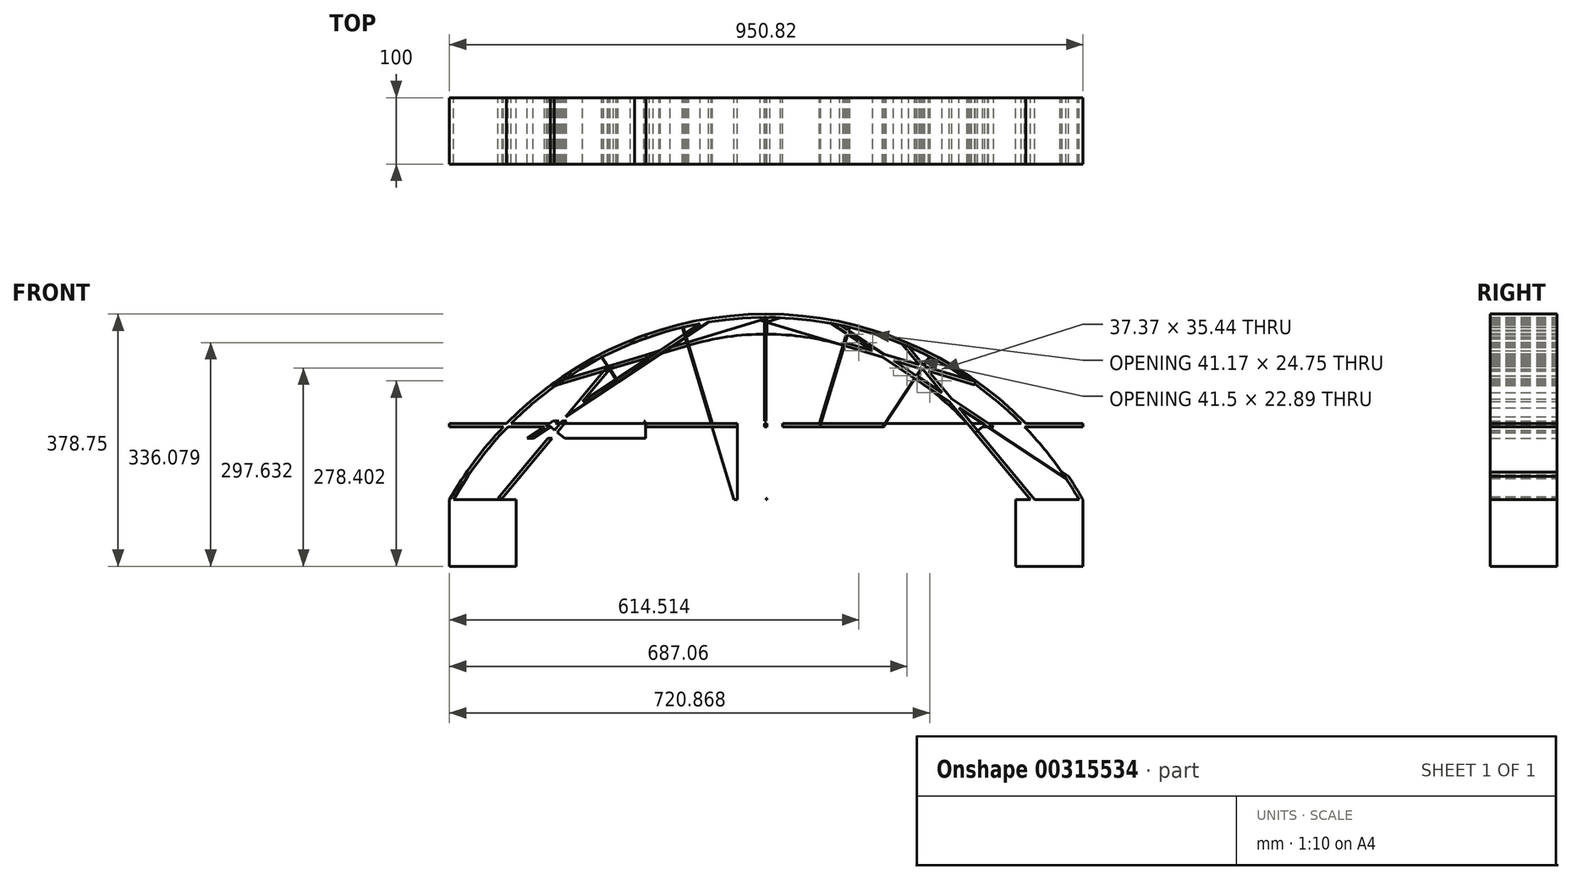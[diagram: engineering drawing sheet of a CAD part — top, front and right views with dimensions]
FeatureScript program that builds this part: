
annotation { "Feature Type Name" : "Feature", "Feature Type Description" : "" }
export const myFeature = defineFeature(function(context is Context, id is Id, definition is map)
    precondition{}
    {
        {
            var Q0;
            Q0=qCreatedBy(makeId("Front.planeOp"),FACE);
            var sketch = newSketch(context, id + "F0", { "sketchPlane" : qUnion([Q0])});
            skLineSegment(sketch, "E0.bottom", {"start": v(0, 85.96) * mm, "end": v(-100, 85.96) * mm});
            skLineSegment(sketch, "E0.top", {"start": v(0, 185.96) * mm, "end": v(-100, 185.96) * mm});
            skLineSegment(sketch, "E0.left", {"start": v(0, 85.96) * mm, "end": v(0, 185.96) * mm});
            skLineSegment(sketch, "E0.right", {"start": v(-100, 85.96) * mm, "end": v(-100, 185.96) * mm});
            skPoint(sketch, "E0.middle", {"position": v(-50, 135.96) * mm});
            skLineSegment(sketch, "E1", {"start": v(0, 185.96) * mm, "end": v(375, 185.96) * mm});
            skLineSegment(sketch, "E2", {"start": v(375, 185.96) * mm, "end": v(750, 185.96) * mm});
            skLineSegment(sketch, "E3.bottom", {"start": v(750, 185.96) * mm, "end": v(850.82, 185.96) * mm});
            skLineSegment(sketch, "E3.top", {"start": v(750, 85.96) * mm, "end": v(850.82, 85.96) * mm});
            skLineSegment(sketch, "E3.left", {"start": v(750, 185.96) * mm, "end": v(750, 85.96) * mm});
            skLineSegment(sketch, "E3.right", {"start": v(850.82, 185.96) * mm, "end": v(850.82, 85.96) * mm});
            skArc(sketch, "E4", {"start": v(750, 185.96) * mm, "mid": v(375, 434.6) * mm, "end": v(0, 185.96) * mm});
            skArc(sketch, "E5", {"start": v(850.82, 185.96) * mm, "mid": v(375.41, 464.71) * mm, "end": v(-100, 185.96) * mm});
            skLineSegment(sketch, "E6", {"start": v(-100, 295.5) * mm, "end": v(850.82, 295.5) * mm});
            skLineSegment(sketch, "E7", {"start": v(850.82, 295.5) * mm, "end": v(850.82, 300.5) * mm});
            skLineSegment(sketch, "E8", {"start": v(850.82, 300.5) * mm, "end": v(-100, 300.5) * mm});
            skLineSegment(sketch, "E9", {"start": v(-100, 300.5) * mm, "end": v(-100, 295.5) * mm});
            skLineSegment(sketch, "E10", {"start": v(375, 27.5) * mm, "end": v(325, 27.5) * mm});
            skLineSegment(sketch, "E11", {"start": v(375, 27.5) * mm, "end": v(425, 27.5) * mm});
            skLineSegment(sketch, "E12", {"start": v(375, 27.5) * mm, "end": v(0, 185.96) * mm});
            skLineSegment(sketch, "E13", {"start": v(375, 27.5) * mm, "end": v(318.99, 73.97) * mm});
            skLineSegment(sketch, "E14", {"start": v(375, 27.5) * mm, "end": v(339.38, 81.23) * mm});
            skLineSegment(sketch, "E15", {"start": v(375, 27.5) * mm, "end": v(354.37, 95.94) * mm});
            skLineSegment(sketch, "E16", {"start": v(375, 27.5) * mm, "end": v(375, 108.9) * mm});
            skLineSegment(sketch, "E17", {"start": v(318.99, 73.97) * mm, "end": v(13.67, 327.28) * mm});
            skLineSegment(sketch, "E18", {"start": v(339.38, 81.23) * mm, "end": v(125.4, 403.95) * mm});
            skLineSegment(sketch, "E19", {"start": v(354.37, 95.94) * mm, "end": v(247.79, 449.55) * mm});
            skLineSegment(sketch, "E20", {"start": v(375, 108.9) * mm, "end": v(375, 464.71) * mm});
            skLineSegment(sketch, "E21", {"start": v(61.68, 287.44) * mm, "end": v(-22.5, 185.96) * mm});
            skLineSegment(sketch, "E22", {"start": v(61.68, 287.44) * mm, "end": v(178.05, 427.7) * mm});
            skLineSegment(sketch, "E23", {"start": v(150.03, 366.8) * mm, "end": v(-85.2, 210.82) * mm});
            skLineSegment(sketch, "E24", {"start": v(257.51, 417.29) * mm, "end": v(45.34, 353.33) * mm});
            skLineSegment(sketch, "E25", {"start": v(257.51, 417.29) * mm, "end": v(411, 463.55) * mm});
            skLineSegment(sketch, "E26", {"start": v(375, 452.7) * mm, "end": v(706.03, 352.92) * mm});
            skLineSegment(sketch, "E27", {"start": v(375, 452.7) * mm, "end": v(339.15, 463.5) * mm});
            skLineSegment(sketch, "E28", {"start": v(572.77, 427.7) * mm, "end": v(771.91, 185.96) * mm});
            skLineSegment(sketch, "E29", {"start": v(836.03, 210.82) * mm, "end": v(462.36, 457.73) * mm});
            skLineSegment(sketch, "E30", {"start": v(492.49, 417.29) * mm, "end": v(375, 27.5) * mm});
            skLineSegment(sketch, "E31", {"start": v(375, 27.5) * mm, "end": v(624.17, 404.6) * mm});
            skLineSegment(sketch, "E32", {"start": v(375, 27.5) * mm, "end": v(738, 326.53) * mm});
            skLineSegment(sketch, "E33", {"start": v(375, 27.5) * mm, "end": v(750, 185.96) * mm});
            skLineSegment(sketch, "E34", {"start": v(-22.5, 185.96) * mm, "end": v(-26.35, 189.15) * mm});
            skLineSegment(sketch, "E35", {"start": v(-26.35, 189.15) * mm, "end": v(168.33, 423.82) * mm});
            skLineSegment(sketch, "E36", {"start": v(168.33, 423.82) * mm, "end": v(-29, 185.96) * mm});
            skLineSegment(sketch, "E37", {"start": v(-85.2, 210.82) * mm, "end": v(-82.44, 206.66) * mm});
            skLineSegment(sketch, "E38", {"start": v(-82.44, 206.66) * mm, "end": v(298.52, 459.26) * mm});
            skLineSegment(sketch, "E39", {"start": v(150.03, 366.8) * mm, "end": v(286.74, 457.45) * mm});
            skLineSegment(sketch, "E40", {"start": v(-82.44, 206.66) * mm, "end": v(-91.46, 200.68) * mm});
            skLineSegment(sketch, "E41", {"start": v(69.56, 360.64) * mm, "end": v(68.12, 365.42) * mm});
            skLineSegment(sketch, "E42", {"start": v(68.12, 365.42) * mm, "end": v(396.21, 464.32) * mm});
            skLineSegment(sketch, "E43", {"start": v(396.21, 464.32) * mm, "end": v(57.23, 362.14) * mm});
            skLineSegment(sketch, "E44", {"start": v(688.37, 358.25) * mm, "end": v(689.8, 363.03) * mm});
            skLineSegment(sketch, "E45", {"start": v(689.8, 363.03) * mm, "end": v(694.18, 361.72) * mm});
            skLineSegment(sketch, "E46", {"start": v(694.18, 361.72) * mm, "end": v(353.88, 464.29) * mm});
            skLineSegment(sketch, "E47", {"start": v(816.74, 223.57) * mm, "end": v(819.5, 227.74) * mm});
            skLineSegment(sketch, "E48", {"start": v(819.5, 227.74) * mm, "end": v(829.25, 221.3) * mm});
            skLineSegment(sketch, "E49", {"start": v(829.25, 221.3) * mm, "end": v(474.65, 455.6) * mm});
            skLineSegment(sketch, "E50", {"start": v(763.23, 196.5) * mm, "end": v(767.1, 199.68) * mm});
            skLineSegment(sketch, "E51", {"start": v(767.1, 199.68) * mm, "end": v(778.4, 185.96) * mm});
            skLineSegment(sketch, "E52", {"start": v(778.4, 185.96) * mm, "end": v(582.43, 423.85) * mm});
            skLineSegment(sketch, "E53", {"start": v(0, 185.96) * mm, "end": v(-4.6, 187.9) * mm});
            skLineSegment(sketch, "E54", {"start": v(750, 185.96) * mm, "end": v(754.6, 187.9) * mm});
            skLineSegment(sketch, "E55", {"start": v(-98.5, 188.61) * mm, "end": v(-94.02, 186.4) * mm});
            skLineSegment(sketch, "E56", {"start": v(375, 464.71) * mm, "end": v(375, 459.71) * mm});
            skLineSegment(sketch, "E57", {"start": v(846.68, 193.24) * mm, "end": v(842.5, 190.5) * mm});
            skArc(sketch, "E58", {"start": v(842.5, 190.5) * mm, "mid": v(373.05, 459.7) * mm, "end": v(-94.02, 186.4) * mm});
            skLineSegment(sketch, "E59", {"start": v(842.5, 190.5) * mm, "end": v(845.47, 185.96) * mm});
            skLineSegment(sketch, "E60", {"start": v(-94.02, 186.4) * mm, "end": v(-94.24, 185.96) * mm});
            skLineSegment(sketch, "E61", {"start": v(372.99, 188.16) * mm, "end": v(376.3, 188.16) * mm});
            skLineSegment(sketch, "E62", {"start": v(376.3, 188.16) * mm, "end": v(376.3, 464.71) * mm});
            skLineSegment(sketch, "E63", {"start": v(376.3, 464.71) * mm, "end": v(376.3, 185.96) * mm});
            skLineSegment(sketch, "E64", {"start": v(376.3, 185.96) * mm, "end": v(372.99, 185.96) * mm});
            skLineSegment(sketch, "E65", {"start": v(372.99, 185.96) * mm, "end": v(372.99, 464.7) * mm});
            skLineSegment(sketch, "E66", {"start": v(420.7, 185.96) * mm, "end": v(500.35, 450.2) * mm});
            skLineSegment(sketch, "E67", {"start": v(492.49, 417.29) * mm, "end": v(502.4, 450.2) * mm});
            skLineSegment(sketch, "E68", {"start": v(477.93, 185.96) * mm, "end": v(622.85, 405.28) * mm});
            skLineSegment(sketch, "E69", {"start": v(294.52, 300.5) * mm, "end": v(249.59, 449.55) * mm});
            skLineSegment(sketch, "E70", {"start": v(194.9, 300.5) * mm, "end": v(126.07, 404.3) * mm});
            skLineSegment(sketch, "E71", {"start": v(400, 27.5) * mm, "end": v(400, 434.6) * mm});
            skPoint(sketch, "E71.endSnap0", {"position": v(375, 434.6) * mm});
            skLineSegment(sketch, "E72", {"start": v(415.27, 434.6) * mm, "end": v(415.27, 185.96) * mm});
            skLineSegment(sketch, "E73", {"start": v(194.97, -80.07) * mm, "end": v(194.97, 464.71) * mm});
            skLineSegment(sketch, "E74", {"start": v(292.72, 300.5) * mm, "end": v(292.72, 278.2) * mm});
            skLineSegment(sketch, "E75", {"start": v(375, 278.2) * mm, "end": v(292.72, 278.2) * mm});
            skLineSegment(sketch, "E76", {"start": v(194, 300.5) * mm, "end": v(194, 278.2) * mm});
            skLineSegment(sketch, "E77", {"start": v(292.72, 278.2) * mm, "end": v(194, 278.2) * mm});
            skLineSegment(sketch, "E78", {"start": v(45.95, 300.5) * mm, "end": v(45.95, 278.2) * mm});
            skLineSegment(sketch, "E79", {"start": v(45.95, 278.2) * mm, "end": v(194, 278.2) * mm});
            skLineSegment(sketch, "E80", {"start": v(-100, 295.5) * mm, "end": v(-100, 278.2) * mm});
            skLineSegment(sketch, "E81", {"start": v(-100, 278.2) * mm, "end": v(45.95, 278.2) * mm});
            skLineSegment(sketch, "E82", {"start": v(332.4, 300.5) * mm, "end": v(332.4, 185.96) * mm});
            skLineSegment(sketch, "E83", {"start": v(375, 304.05) * mm, "end": v(-10.9, 304.05) * mm});
            skLineSegment(sketch, "E84", {"start": v(-22.5, 189.52) * mm, "end": v(0, 189.52) * mm});
            skLineSegment(sketch, "E85", {"start": v(-82.44, 188.18) * mm, "end": v(0, 188.18) * mm});
            skLineSegment(sketch, "E86", {"start": v(60.02, 358) * mm, "end": v(0, 358) * mm});
            skSolve(sketch);
        }
        {
            var Q0;
            {var subQ5=sQuery(id+"F0.wireOp",EDGE,"E7");Q0=makeQuery(id+"F0.imprint","IMPRINT",FACE,{"disambiguationData":[TD([[makeQuery(id+"F0.imprint","IMPRINT",EDGE,{"derivedFrom":subQ5}),1.0]])]});}
            var Q1;
            {var subQ5=sQuery(id+"F0.wireOp",EDGE,"E9");Q1=makeQuery(id+"F0.imprint","IMPRINT",FACE,{"disambiguationData":[TD([[makeQuery(id+"F0.imprint","IMPRINT",EDGE,{"derivedFrom":subQ5}),1.0]])]});}
            var Q2;
            {var subQ0=sQuery(id+"F0.wireOp",EDGE,"E37");Q2=makeQuery(id+"F0.imprint","IMPRINT",FACE,{"disambiguationData":[TD([[makeQuery(id+"F0.imprint","IMPRINT",EDGE,{"derivedFrom":subQ0}),-1.0]])]});}
            var Q3;
            {var subQ4=sQuery(id+"F0.wireOp",EDGE,"E55");Q3=makeQuery(id+"F0.imprint","IMPRINT",FACE,{"disambiguationData":[TD([[makeQuery(id+"F0.imprint","IMPRINT",EDGE,{"derivedFrom":subQ4}),-1.0]])]});}
            var Q4;
            {var subQ4=sQuery(id+"F0.wireOp",EDGE,"E57");Q4=makeQuery(id+"F0.imprint","IMPRINT",FACE,{"disambiguationData":[TD([[makeQuery(id+"F0.imprint","IMPRINT",EDGE,{"derivedFrom":subQ4}),1.0]])]});}
            var Q5;
            {var subQ3=sQuery(id+"F0.wireOp",EDGE,"E57");Q5=makeQuery(id+"F0.imprint","IMPRINT",FACE,{"disambiguationData":[TD([[makeQuery(id+"F0.imprint","IMPRINT",EDGE,{"derivedFrom":subQ3}),-1.0]])]});}
            var Q6;
            {var subQ0=sQuery(id+"F0.wireOp",EDGE,"E32");var subQ1=sQuery(id+"F0.wireOp",EDGE,"E5");var subQ2=makeQuery(id+"F0.imprint","INTERSECT",VERTEX,{"derivedFrom":[subQ1,subQ0]});Q6=makeQuery(id+"F0.imprint","IMPRINT",FACE,{"disambiguationData":[TD([[makeQuery(id+"F0.imprint","IMPRINT",EDGE,{"disambiguationData":[TD([[subQ2,1.0]])],"derivedFrom":subQ1}),1.0]])]});}
            var Q7;
            {var subQ0=sQuery(id+"F0.wireOp",EDGE,"E26");var subQ1=sQuery(id+"F0.wireOp",EDGE,"E5");var subQ2=makeQuery(id+"F0.imprint","INTERSECT",VERTEX,{"derivedFrom":[subQ1,subQ0]});Q7=makeQuery(id+"F0.imprint","IMPRINT",FACE,{"disambiguationData":[TD([[makeQuery(id+"F0.imprint","IMPRINT",EDGE,{"disambiguationData":[TD([[subQ2,1.0]])],"derivedFrom":subQ1}),1.0]])]});}
            var Q8;
            {var subQ0=sQuery(id+"F0.wireOp",EDGE,"E31");var subQ1=sQuery(id+"F0.wireOp",EDGE,"E5");var subQ2=makeQuery(id+"F0.imprint","INTERSECT",VERTEX,{"derivedFrom":[subQ1,subQ0]});Q8=makeQuery(id+"F0.imprint","IMPRINT",FACE,{"disambiguationData":[TD([[makeQuery(id+"F0.imprint","IMPRINT",EDGE,{"disambiguationData":[TD([[subQ2,-1.0]])],"derivedFrom":subQ1}),1.0]])]});}
            var Q9;
            {var subQ0=sQuery(id+"F0.wireOp",EDGE,"E52");var subQ1=sQuery(id+"F0.wireOp",EDGE,"E5");var subQ2=makeQuery(id+"F0.imprint","INTERSECT",VERTEX,{"derivedFrom":[subQ1,subQ0]});Q9=makeQuery(id+"F0.imprint","IMPRINT",FACE,{"disambiguationData":[TD([[makeQuery(id+"F0.imprint","IMPRINT",EDGE,{"disambiguationData":[TD([[subQ2,1.0]])],"derivedFrom":subQ1}),1.0]])]});}
            var Q10;
            {var subQ0=sQuery(id+"F0.wireOp",EDGE,"E28");var subQ1=sQuery(id+"F0.wireOp",EDGE,"E5");var subQ2=makeQuery(id+"F0.imprint","INTERSECT",VERTEX,{"derivedFrom":[subQ1,subQ0]});Q10=makeQuery(id+"F0.imprint","IMPRINT",FACE,{"disambiguationData":[TD([[makeQuery(id+"F0.imprint","IMPRINT",EDGE,{"disambiguationData":[TD([[subQ2,1.0]])],"derivedFrom":subQ1}),1.0]])]});}
            var Q11;
            {var subQ0=sQuery(id+"F0.wireOp",EDGE,"E28");var subQ1=sQuery(id+"F0.wireOp",EDGE,"E5");var subQ2=makeQuery(id+"F0.imprint","INTERSECT",VERTEX,{"derivedFrom":[subQ1,subQ0]});Q11=makeQuery(id+"F0.imprint","IMPRINT",FACE,{"disambiguationData":[TD([[makeQuery(id+"F0.imprint","IMPRINT",EDGE,{"disambiguationData":[TD([[subQ2,-1.0]])],"derivedFrom":subQ1}),1.0]])]});}
            var Q12;
            {var subQ0=sQuery(id+"F0.wireOp",EDGE,"E66");var subQ1=sQuery(id+"F0.wireOp",EDGE,"E5");var subQ2=makeQuery(id+"F0.imprint","INTERSECT",VERTEX,{"derivedFrom":[subQ1,subQ0]});Q12=makeQuery(id+"F0.imprint","IMPRINT",FACE,{"disambiguationData":[TD([[makeQuery(id+"F0.imprint","IMPRINT",EDGE,{"disambiguationData":[TD([[subQ2,1.0]])],"derivedFrom":subQ1}),1.0]])]});}
            var Q13;
            {var subQ0=sQuery(id+"F0.wireOp",EDGE,"E49");var subQ1=sQuery(id+"F0.wireOp",EDGE,"E5");var subQ2=makeQuery(id+"F0.imprint","INTERSECT",VERTEX,{"disambiguationData":[OD(1.0)],"derivedFrom":[subQ1,subQ0]});Q13=makeQuery(id+"F0.imprint","IMPRINT",FACE,{"disambiguationData":[TD([[makeQuery(id+"F0.imprint","IMPRINT",EDGE,{"disambiguationData":[TD([[subQ2,1.0]])],"derivedFrom":subQ1}),1.0]])]});}
            var Q14;
            {var subQ0=sQuery(id+"F0.wireOp",EDGE,"E29");var subQ1=sQuery(id+"F0.wireOp",EDGE,"E5");var subQ2=makeQuery(id+"F0.imprint","INTERSECT",VERTEX,{"disambiguationData":[OD(1.0)],"derivedFrom":[subQ1,subQ0]});Q14=makeQuery(id+"F0.imprint","IMPRINT",FACE,{"disambiguationData":[TD([[makeQuery(id+"F0.imprint","IMPRINT",EDGE,{"disambiguationData":[TD([[subQ2,1.0]])],"derivedFrom":subQ1}),1.0]])]});}
            var Q15;
            {var subQ0=sQuery(id+"F0.wireOp",EDGE,"E25");var subQ1=sQuery(id+"F0.wireOp",EDGE,"E5");var subQ2=makeQuery(id+"F0.imprint","INTERSECT",VERTEX,{"derivedFrom":[subQ1,subQ0]});Q15=makeQuery(id+"F0.imprint","IMPRINT",FACE,{"disambiguationData":[TD([[makeQuery(id+"F0.imprint","IMPRINT",EDGE,{"disambiguationData":[TD([[subQ2,1.0]])],"derivedFrom":subQ1}),1.0]])]});}
            var Q16;
            {var subQ0=sQuery(id+"F0.wireOp",EDGE,"E25");var subQ1=sQuery(id+"F0.wireOp",EDGE,"E5");var subQ2=makeQuery(id+"F0.imprint","INTERSECT",VERTEX,{"derivedFrom":[subQ1,subQ0]});Q16=makeQuery(id+"F0.imprint","IMPRINT",FACE,{"disambiguationData":[TD([[makeQuery(id+"F0.imprint","IMPRINT",EDGE,{"disambiguationData":[TD([[subQ2,-1.0]])],"derivedFrom":subQ1}),1.0]])]});}
            var Q17;
            {var subQ0=sQuery(id+"F0.wireOp",EDGE,"E43");var subQ1=sQuery(id+"F0.wireOp",EDGE,"E5");var subQ2=makeQuery(id+"F0.imprint","INTERSECT",VERTEX,{"disambiguationData":[OD(0.0)],"derivedFrom":[subQ1,subQ0]});Q17=makeQuery(id+"F0.imprint","IMPRINT",FACE,{"disambiguationData":[TD([[makeQuery(id+"F0.imprint","IMPRINT",EDGE,{"disambiguationData":[TD([[subQ2,-1.0]])],"derivedFrom":subQ1}),1.0]])]});}
            var Q18;
            {var subQ0=sQuery(id+"F0.wireOp",EDGE,"E56");Q18=makeQuery(id+"F0.imprint","IMPRINT",FACE,{"disambiguationData":[TD([[makeQuery(id+"F0.imprint","IMPRINT",EDGE,{"derivedFrom":subQ0}),1.0]])]});}
            var Q19;
            {var subQ0=sQuery(id+"F0.wireOp",EDGE,"E56");Q19=makeQuery(id+"F0.imprint","IMPRINT",FACE,{"disambiguationData":[TD([[makeQuery(id+"F0.imprint","IMPRINT",EDGE,{"derivedFrom":subQ0}),-1.0]])]});}
            var Q20;
            {var subQ0=sQuery(id+"F0.wireOp",EDGE,"E46");var subQ1=sQuery(id+"F0.wireOp",EDGE,"E5");var subQ2=makeQuery(id+"F0.imprint","INTERSECT",VERTEX,{"disambiguationData":[OD(1.0)],"derivedFrom":[subQ1,subQ0]});Q20=makeQuery(id+"F0.imprint","IMPRINT",FACE,{"disambiguationData":[TD([[makeQuery(id+"F0.imprint","IMPRINT",EDGE,{"disambiguationData":[TD([[subQ2,1.0]])],"derivedFrom":subQ1}),1.0]])]});}
            var Q21;
            {var subQ0=sQuery(id+"F0.wireOp",EDGE,"E27");var subQ1=sQuery(id+"F0.wireOp",EDGE,"E5");var subQ2=makeQuery(id+"F0.imprint","INTERSECT",VERTEX,{"derivedFrom":[subQ1,subQ0]});Q21=makeQuery(id+"F0.imprint","IMPRINT",FACE,{"disambiguationData":[TD([[makeQuery(id+"F0.imprint","IMPRINT",EDGE,{"disambiguationData":[TD([[subQ2,1.0]])],"derivedFrom":subQ1}),1.0]])]});}
            var Q22;
            {var subQ0=sQuery(id+"F0.wireOp",EDGE,"E27");var subQ1=sQuery(id+"F0.wireOp",EDGE,"E5");var subQ2=makeQuery(id+"F0.imprint","INTERSECT",VERTEX,{"derivedFrom":[subQ1,subQ0]});Q22=makeQuery(id+"F0.imprint","IMPRINT",FACE,{"disambiguationData":[TD([[makeQuery(id+"F0.imprint","IMPRINT",EDGE,{"disambiguationData":[TD([[subQ2,-1.0]])],"derivedFrom":subQ1}),1.0]])]});}
            var Q23;
            {var subQ0=sQuery(id+"F0.wireOp",EDGE,"E38");var subQ1=sQuery(id+"F0.wireOp",EDGE,"E5");var subQ2=makeQuery(id+"F0.imprint","INTERSECT",VERTEX,{"derivedFrom":[subQ1,subQ0]});Q23=makeQuery(id+"F0.imprint","IMPRINT",FACE,{"disambiguationData":[TD([[makeQuery(id+"F0.imprint","IMPRINT",EDGE,{"disambiguationData":[TD([[subQ2,-1.0]])],"derivedFrom":subQ1}),1.0]])]});}
            var Q24;
            {var subQ0=sQuery(id+"F0.wireOp",EDGE,"E19");var subQ1=sQuery(id+"F0.wireOp",EDGE,"E5");var subQ2=makeQuery(id+"F0.imprint","INTERSECT",VERTEX,{"derivedFrom":[subQ1,subQ0]});Q24=makeQuery(id+"F0.imprint","IMPRINT",FACE,{"disambiguationData":[TD([[makeQuery(id+"F0.imprint","IMPRINT",EDGE,{"disambiguationData":[TD([[subQ2,-1.0]])],"derivedFrom":subQ1}),1.0]])]});}
            var Q25;
            {var subQ0=sQuery(id+"F0.wireOp",EDGE,"E22");var subQ1=sQuery(id+"F0.wireOp",EDGE,"E5");var subQ2=makeQuery(id+"F0.imprint","INTERSECT",VERTEX,{"derivedFrom":[subQ1,subQ0]});Q25=makeQuery(id+"F0.imprint","IMPRINT",FACE,{"disambiguationData":[TD([[makeQuery(id+"F0.imprint","IMPRINT",EDGE,{"disambiguationData":[TD([[subQ2,-1.0]])],"derivedFrom":subQ1}),1.0]])]});}
            var Q26;
            {var subQ0=sQuery(id+"F0.wireOp",EDGE,"E36");var subQ1=sQuery(id+"F0.wireOp",EDGE,"E5");var subQ2=makeQuery(id+"F0.imprint","INTERSECT",VERTEX,{"derivedFrom":[subQ1,subQ0]});Q26=makeQuery(id+"F0.imprint","IMPRINT",FACE,{"disambiguationData":[TD([[makeQuery(id+"F0.imprint","IMPRINT",EDGE,{"disambiguationData":[TD([[subQ2,-1.0]])],"derivedFrom":subQ1}),1.0]])]});}
            var Q27;
            {var subQ0=sQuery(id+"F0.wireOp",EDGE,"E18");var subQ1=sQuery(id+"F0.wireOp",EDGE,"E5");var subQ2=makeQuery(id+"F0.imprint","INTERSECT",VERTEX,{"derivedFrom":[subQ1,subQ0]});Q27=makeQuery(id+"F0.imprint","IMPRINT",FACE,{"disambiguationData":[TD([[makeQuery(id+"F0.imprint","IMPRINT",EDGE,{"disambiguationData":[TD([[subQ2,1.0]])],"derivedFrom":subQ1}),1.0]])]});}
            var Q28;
            {var subQ0=sQuery(id+"F0.wireOp",EDGE,"E17");var subQ1=sQuery(id+"F0.wireOp",EDGE,"E5");var subQ2=makeQuery(id+"F0.imprint","INTERSECT",VERTEX,{"derivedFrom":[subQ1,subQ0]});Q28=makeQuery(id+"F0.imprint","IMPRINT",FACE,{"disambiguationData":[TD([[makeQuery(id+"F0.imprint","IMPRINT",EDGE,{"disambiguationData":[TD([[subQ2,1.0]])],"derivedFrom":subQ1}),1.0]])]});}
            var Q29;
            {var subQ0=sQuery(id+"F0.wireOp",EDGE,"E17");var subQ1=sQuery(id+"F0.wireOp",EDGE,"E5");var subQ2=makeQuery(id+"F0.imprint","INTERSECT",VERTEX,{"derivedFrom":[subQ1,subQ0]});Q29=makeQuery(id+"F0.imprint","IMPRINT",FACE,{"disambiguationData":[TD([[makeQuery(id+"F0.imprint","IMPRINT",EDGE,{"disambiguationData":[TD([[subQ2,-1.0]])],"derivedFrom":subQ1}),1.0]])]});}
            var Q30;
            {var subQ1=sQuery(id+"F0.wireOp",EDGE,"E5");var subQ3=sQuery(id+"F0.wireOp",EDGE,"E6");var subQ4=makeQuery(id+"F0.imprint","INTERSECT",VERTEX,{"disambiguationData":[OD(1.0)],"derivedFrom":[subQ1,subQ3]});Q30=makeQuery(id+"F0.imprint","IMPRINT",FACE,{"disambiguationData":[TD([[makeQuery(id+"F0.imprint","IMPRINT",EDGE,{"disambiguationData":[TD([[subQ4,-1.0]])],"derivedFrom":subQ3}),-1.0]])]});}
            var Q31;
            Q31=makeQuery(id+"F0.imprint","IMPRINT",FACE,{"disambiguationData":[TD([[makeQuery(id+"F0.imprint","IMPRINT",EDGE,{"derivedFrom":sQuery(id+"F0.wireOp",EDGE,"E0.bottom")}),-1.0]])]});
            var Q32;
            Q32=makeQuery(id+"F0.imprint","IMPRINT",FACE,{"disambiguationData":[TD([[makeQuery(id+"F0.imprint","IMPRINT",EDGE,{"derivedFrom":sQuery(id+"F0.wireOp",EDGE,"E3.top")}),1.0]])]});
            var Q33;
            {var subQ3=sQuery(id+"F0.wireOp",EDGE,"E5");var subQ7=sQuery(id+"F0.wireOp",EDGE,"E29");var subQ9=makeQuery(id+"F0.imprint","INTERSECT",VERTEX,{"disambiguationData":[OD(0.0)],"derivedFrom":[subQ3,subQ7]});Q33=makeQuery(id+"F0.imprint","IMPRINT",FACE,{"disambiguationData":[TD([[makeQuery(id+"F0.imprint","IMPRINT",EDGE,{"disambiguationData":[TD([[subQ9,-1.0]])],"derivedFrom":subQ3}),1.0]])]});}
            var Q34;
            {var subQ0=sQuery(id+"F0.wireOp",EDGE,"E49");var subQ6=sQuery(id+"F0.wireOp",EDGE,"E5");var subQ7=makeQuery(id+"F0.imprint","INTERSECT",VERTEX,{"disambiguationData":[OD(0.0)],"derivedFrom":[subQ6,subQ0]});Q34=makeQuery(id+"F0.imprint","IMPRINT",FACE,{"disambiguationData":[TD([[makeQuery(id+"F0.imprint","IMPRINT",EDGE,{"disambiguationData":[TD([[subQ7,-1.0]])],"derivedFrom":subQ6}),1.0]])]});}
            var Q35;
            {var subQ0=sQuery(id+"F0.wireOp",EDGE,"E6");var subQ1=sQuery(id+"F0.wireOp",EDGE,"E5");var subQ2=makeQuery(id+"F0.imprint","INTERSECT",VERTEX,{"disambiguationData":[OD(0.0)],"derivedFrom":[subQ1,subQ0]});Q35=makeQuery(id+"F0.imprint","IMPRINT",FACE,{"disambiguationData":[TD([[makeQuery(id+"F0.imprint","IMPRINT",EDGE,{"disambiguationData":[TD([[subQ2,-1.0]])],"derivedFrom":subQ1}),1.0]])]});}
            var Q36;
            {var subQ3=sQuery(id+"F0.wireOp",EDGE,"E5");var subQ7=sQuery(id+"F0.wireOp",EDGE,"E26");var subQ8=makeQuery(id+"F0.imprint","INTERSECT",VERTEX,{"derivedFrom":[subQ3,subQ7]});Q36=makeQuery(id+"F0.imprint","IMPRINT",FACE,{"disambiguationData":[TD([[makeQuery(id+"F0.imprint","IMPRINT",EDGE,{"disambiguationData":[TD([[subQ8,-1.0]])],"derivedFrom":subQ3}),1.0]])]});}
            var Q37;
            {var subQ4=sQuery(id+"F0.wireOp",EDGE,"E5");var subQ6=sQuery(id+"F0.wireOp",EDGE,"E31");var subQ7=makeQuery(id+"F0.imprint","INTERSECT",VERTEX,{"derivedFrom":[subQ4,subQ6]});Q37=makeQuery(id+"F0.imprint","IMPRINT",FACE,{"disambiguationData":[TD([[makeQuery(id+"F0.imprint","IMPRINT",EDGE,{"disambiguationData":[TD([[subQ7,1.0]])],"derivedFrom":subQ4}),1.0]])]});}
            var Q38;
            {var subQ4=sQuery(id+"F0.wireOp",EDGE,"E19");var subQ5=sQuery(id+"F0.wireOp",EDGE,"E5");var subQ6=makeQuery(id+"F0.imprint","INTERSECT",VERTEX,{"derivedFrom":[subQ5,subQ4]});Q38=makeQuery(id+"F0.imprint","IMPRINT",FACE,{"disambiguationData":[TD([[makeQuery(id+"F0.imprint","IMPRINT",EDGE,{"disambiguationData":[TD([[subQ6,1.0]])],"derivedFrom":subQ5}),1.0]])]});}
            var Q39;
            {var subQ2=sQuery(id+"F0.wireOp",EDGE,"E5");var subQ6=sQuery(id+"F0.wireOp",EDGE,"E18");var subQ7=makeQuery(id+"F0.imprint","INTERSECT",VERTEX,{"derivedFrom":[subQ2,subQ6]});Q39=makeQuery(id+"F0.imprint","IMPRINT",FACE,{"disambiguationData":[TD([[makeQuery(id+"F0.imprint","IMPRINT",EDGE,{"disambiguationData":[TD([[subQ7,-1.0]])],"derivedFrom":subQ2}),1.0]])]});}
            var Q40;
            {var subQ3=sQuery(id+"F0.wireOp",EDGE,"E5");var subQ7=sQuery(id+"F0.wireOp",EDGE,"E24");var subQ8=makeQuery(id+"F0.imprint","INTERSECT",VERTEX,{"derivedFrom":[subQ3,subQ7]});Q40=makeQuery(id+"F0.imprint","IMPRINT",FACE,{"disambiguationData":[TD([[makeQuery(id+"F0.imprint","IMPRINT",EDGE,{"disambiguationData":[TD([[subQ8,1.0]])],"derivedFrom":subQ3}),1.0]])]});}
            var Q41;
            {var subQ0=sQuery(id+"F0.wireOp",EDGE,"E8");var subQ1=sQuery(id+"F0.wireOp",EDGE,"E5");var subQ2=makeQuery(id+"F0.imprint","INTERSECT",VERTEX,{"disambiguationData":[OD(1.0)],"derivedFrom":[subQ1,subQ0]});Q41=makeQuery(id+"F0.imprint","IMPRINT",FACE,{"disambiguationData":[TD([[makeQuery(id+"F0.imprint","IMPRINT",EDGE,{"disambiguationData":[TD([[subQ2,-1.0]])],"derivedFrom":subQ1}),1.0]])]});}
            var Q42;
            {var subQ0=sQuery(id+"F0.wireOp",EDGE,"E40");Q42=makeQuery(id+"F0.imprint","IMPRINT",FACE,{"disambiguationData":[TD([[makeQuery(id+"F0.imprint","IMPRINT",EDGE,{"derivedFrom":subQ0}),1.0]])]});}
            var Q43;
            {var subQ0=sQuery(id+"F0.wireOp",EDGE,"E37");Q43=makeQuery(id+"F0.imprint","IMPRINT",FACE,{"disambiguationData":[TD([[makeQuery(id+"F0.imprint","IMPRINT",EDGE,{"derivedFrom":subQ0}),1.0]])]});}
            var Q44;
            {var subQ0=sQuery(id+"F0.wireOp",EDGE,"E23");var subQ1=sQuery(id+"F0.wireOp",EDGE,"E6");var subQ2=makeQuery(id+"F0.imprint","INTERSECT",VERTEX,{"derivedFrom":[subQ1,subQ0]});Q44=makeQuery(id+"F0.imprint","IMPRINT",FACE,{"disambiguationData":[TD([[makeQuery(id+"F0.imprint","IMPRINT",EDGE,{"disambiguationData":[TD([[subQ2,-1.0]])],"derivedFrom":subQ1}),-1.0]])]});}
            var Q45;
            {var subQ0=sQuery(id+"F0.wireOp",EDGE,"E21");Q45=makeQuery(id+"F0.imprint","IMPRINT",FACE,{"disambiguationData":[TD([[makeQuery(id+"F0.imprint","IMPRINT",EDGE,{"derivedFrom":subQ0}),-1.0]])]});}
            var Q46;
            {var subQ0=sQuery(id+"F0.wireOp",EDGE,"E34");Q46=makeQuery(id+"F0.imprint","IMPRINT",FACE,{"disambiguationData":[TD([[makeQuery(id+"F0.imprint","IMPRINT",EDGE,{"derivedFrom":subQ0}),1.0]])]});}
            var Q47;
            {var subQ0=sQuery(id+"F0.wireOp",EDGE,"E36");var subQ1=sQuery(id+"F0.wireOp",EDGE,"E6");var subQ2=makeQuery(id+"F0.imprint","INTERSECT",VERTEX,{"derivedFrom":[subQ1,subQ0]});Q47=makeQuery(id+"F0.imprint","IMPRINT",FACE,{"disambiguationData":[TD([[makeQuery(id+"F0.imprint","IMPRINT",EDGE,{"disambiguationData":[TD([[subQ2,-1.0]])],"derivedFrom":subQ1}),1.0]])]});}
            var Q48;
            {var subQ0=sQuery(id+"F0.wireOp",EDGE,"E36");var subQ1=sQuery(id+"F0.wireOp",EDGE,"E6");var subQ2=makeQuery(id+"F0.imprint","INTERSECT",VERTEX,{"derivedFrom":[subQ1,subQ0]});Q48=makeQuery(id+"F0.imprint","IMPRINT",FACE,{"disambiguationData":[TD([[makeQuery(id+"F0.imprint","IMPRINT",EDGE,{"disambiguationData":[TD([[subQ2,-1.0]])],"derivedFrom":subQ1}),-1.0]])]});}
            var Q49;
            {var subQ1=sQuery(id+"F0.wireOp",EDGE,"E6");var subQ7=sQuery(id+"F0.wireOp",EDGE,"E17");var subQ8=makeQuery(id+"F0.imprint","INTERSECT",VERTEX,{"derivedFrom":[subQ1,subQ7]});Q49=makeQuery(id+"F0.imprint","IMPRINT",FACE,{"disambiguationData":[TD([[makeQuery(id+"F0.imprint","IMPRINT",EDGE,{"disambiguationData":[TD([[subQ8,-1.0]])],"derivedFrom":subQ1}),1.0]])]});}
            var Q50;
            {var subQ0=sQuery(id+"F0.wireOp",EDGE,"E38");var subQ1=sQuery(id+"F0.wireOp",EDGE,"E8");var subQ2=makeQuery(id+"F0.imprint","INTERSECT",VERTEX,{"derivedFrom":[subQ1,subQ0]});Q50=makeQuery(id+"F0.imprint","IMPRINT",FACE,{"disambiguationData":[TD([[makeQuery(id+"F0.imprint","IMPRINT",EDGE,{"disambiguationData":[TD([[subQ2,-1.0]])],"derivedFrom":subQ1}),1.0]])]});}
            var Q51;
            {var subQ0=sQuery(id+"F0.wireOp",EDGE,"E23");var subQ1=sQuery(id+"F0.wireOp",EDGE,"E6");var subQ2=makeQuery(id+"F0.imprint","INTERSECT",VERTEX,{"derivedFrom":[subQ1,subQ0]});Q51=makeQuery(id+"F0.imprint","IMPRINT",FACE,{"disambiguationData":[TD([[makeQuery(id+"F0.imprint","IMPRINT",EDGE,{"disambiguationData":[TD([[subQ2,-1.0]])],"derivedFrom":subQ1}),1.0]])]});}
            var Q52;
            {var subQ1=sQuery(id+"F0.wireOp",EDGE,"E6");var subQ7=sQuery(id+"F0.wireOp",EDGE,"E58");var subQ9=makeQuery(id+"F0.imprint","INTERSECT",VERTEX,{"disambiguationData":[OD(0.0)],"derivedFrom":[subQ1,subQ7]});Q52=makeQuery(id+"F0.imprint","IMPRINT",FACE,{"disambiguationData":[TD([[makeQuery(id+"F0.imprint","IMPRINT",EDGE,{"disambiguationData":[TD([[subQ9,-1.0]])],"derivedFrom":subQ1}),1.0]])]});}
            var Q53;
            {var subQ0=sQuery(id+"F0.wireOp",EDGE,"E23");var subQ1=sQuery(id+"F0.wireOp",EDGE,"E8");var subQ2=makeQuery(id+"F0.imprint","INTERSECT",VERTEX,{"derivedFrom":[subQ1,subQ0]});Q53=makeQuery(id+"F0.imprint","IMPRINT",FACE,{"disambiguationData":[TD([[makeQuery(id+"F0.imprint","IMPRINT",EDGE,{"disambiguationData":[TD([[subQ2,-1.0]])],"derivedFrom":subQ1}),1.0]])]});}
            var Q54;
            {var subQ0=sQuery(id+"F0.wireOp",EDGE,"E38");var subQ1=sQuery(id+"F0.wireOp",EDGE,"E8");var subQ2=makeQuery(id+"F0.imprint","INTERSECT",VERTEX,{"derivedFrom":[subQ1,subQ0]});Q54=makeQuery(id+"F0.imprint","IMPRINT",FACE,{"disambiguationData":[TD([[makeQuery(id+"F0.imprint","IMPRINT",EDGE,{"disambiguationData":[TD([[subQ2,-1.0]])],"derivedFrom":subQ1}),-1.0]])]});}
            var Q55;
            {var subQ0=sQuery(id+"F0.wireOp",EDGE,"E22");var subQ1=sQuery(id+"F0.wireOp",EDGE,"E8");var subQ2=makeQuery(id+"F0.imprint","INTERSECT",VERTEX,{"derivedFrom":[subQ1,subQ0]});Q55=makeQuery(id+"F0.imprint","IMPRINT",FACE,{"disambiguationData":[TD([[makeQuery(id+"F0.imprint","IMPRINT",EDGE,{"disambiguationData":[TD([[subQ2,-1.0]])],"derivedFrom":subQ1}),-1.0]])]});}
            var Q56;
            {var subQ0=sQuery(id+"F0.wireOp",EDGE,"E38");var subQ1=sQuery(id+"F0.wireOp",EDGE,"E22");var subQ2=makeQuery(id+"F0.imprint","INTERSECT",VERTEX,{"derivedFrom":[subQ1,subQ0]});Q56=makeQuery(id+"F0.imprint","IMPRINT",FACE,{"disambiguationData":[TD([[makeQuery(id+"F0.imprint","IMPRINT",EDGE,{"disambiguationData":[TD([[subQ2,-1.0]])],"derivedFrom":subQ1}),1.0]])]});}
            var Q57;
            {var subQ3=sQuery(id+"F0.wireOp",EDGE,"E38");var subQ5=sQuery(id+"F0.wireOp",EDGE,"E22");var subQ7=makeQuery(id+"F0.imprint","INTERSECT",VERTEX,{"derivedFrom":[subQ5,subQ3]});Q57=makeQuery(id+"F0.imprint","IMPRINT",FACE,{"disambiguationData":[TD([[makeQuery(id+"F0.imprint","IMPRINT",EDGE,{"disambiguationData":[TD([[subQ7,-1.0]])],"derivedFrom":subQ5}),-1.0]])]});}
            var Q58;
            {var subQ0=sQuery(id+"F0.wireOp",EDGE,"E18");var subQ1=sQuery(id+"F0.wireOp",EDGE,"E6");var subQ2=makeQuery(id+"F0.imprint","INTERSECT",VERTEX,{"derivedFrom":[subQ1,subQ0]});Q58=makeQuery(id+"F0.imprint","IMPRINT",FACE,{"disambiguationData":[TD([[makeQuery(id+"F0.imprint","IMPRINT",EDGE,{"disambiguationData":[TD([[subQ2,-1.0]])],"derivedFrom":subQ1}),1.0]])]});}
            var Q59;
            {var subQ0=sQuery(id+"F0.wireOp",EDGE,"E19");var subQ1=sQuery(id+"F0.wireOp",EDGE,"E6");var subQ2=makeQuery(id+"F0.imprint","INTERSECT",VERTEX,{"derivedFrom":[subQ1,subQ0]});Q59=makeQuery(id+"F0.imprint","IMPRINT",FACE,{"disambiguationData":[TD([[makeQuery(id+"F0.imprint","IMPRINT",EDGE,{"disambiguationData":[TD([[subQ2,-1.0]])],"derivedFrom":subQ1}),1.0]])]});}
            var Q60;
            {var subQ0=sQuery(id+"F0.wireOp",EDGE,"E8");var subQ1=sQuery(id+"F0.wireOp",EDGE,"E4");var subQ2=makeQuery(id+"F0.imprint","INTERSECT",VERTEX,{"disambiguationData":[OD(1.0)],"derivedFrom":[subQ1,subQ0]});Q60=makeQuery(id+"F0.imprint","IMPRINT",FACE,{"disambiguationData":[TD([[makeQuery(id+"F0.imprint","IMPRINT",EDGE,{"disambiguationData":[TD([[subQ2,-1.0]])],"derivedFrom":subQ1}),1.0]])]});}
            var Q61;
            {var subQ1=sQuery(id+"F0.wireOp",EDGE,"E4");var subQ3=sQuery(id+"F0.wireOp",EDGE,"E38");var subQ4=makeQuery(id+"F0.imprint","INTERSECT",VERTEX,{"disambiguationData":[OD(1.0)],"derivedFrom":[subQ1,subQ3]});Q61=makeQuery(id+"F0.imprint","IMPRINT",FACE,{"disambiguationData":[TD([[makeQuery(id+"F0.imprint","IMPRINT",EDGE,{"disambiguationData":[TD([[subQ4,-1.0]])],"derivedFrom":subQ3}),1.0]])]});}
            var Q62;
            {var subQ5=sQuery(id+"F0.wireOp",EDGE,"E24");var subQ7=sQuery(id+"F0.wireOp",EDGE,"E41");var subQ8=makeQuery(id+"F0.imprint","INTERSECT",VERTEX,{"derivedFrom":[subQ5,subQ7]});Q62=makeQuery(id+"F0.imprint","IMPRINT",FACE,{"disambiguationData":[TD([[makeQuery(id+"F0.imprint","IMPRINT",EDGE,{"disambiguationData":[TD([[subQ8,1.0]])],"derivedFrom":subQ5}),-1.0]])]});}
            var Q63;
            {var subQ0=sQuery(id+"F0.wireOp",EDGE,"E23");var subQ1=sQuery(id+"F0.wireOp",EDGE,"E22");var subQ2=makeQuery(id+"F0.imprint","INTERSECT",VERTEX,{"derivedFrom":[subQ1,subQ0]});Q63=makeQuery(id+"F0.imprint","IMPRINT",FACE,{"disambiguationData":[TD([[makeQuery(id+"F0.imprint","IMPRINT",EDGE,{"disambiguationData":[TD([[subQ2,-1.0]])],"derivedFrom":subQ0}),-1.0]])]});}
            var Q64;
            {var subQ1=sQuery(id+"F0.wireOp",EDGE,"E22");var subQ7=sQuery(id+"F0.wireOp",EDGE,"E43");var subQ8=makeQuery(id+"F0.imprint","INTERSECT",VERTEX,{"derivedFrom":[subQ1,subQ7]});Q64=makeQuery(id+"F0.imprint","IMPRINT",FACE,{"disambiguationData":[TD([[makeQuery(id+"F0.imprint","IMPRINT",EDGE,{"disambiguationData":[TD([[subQ8,-1.0]])],"derivedFrom":subQ1}),1.0]])]});}
            var Q65;
            {var subQ1=sQuery(id+"F0.wireOp",EDGE,"E22");var subQ7=sQuery(id+"F0.wireOp",EDGE,"E70");var subQ8=makeQuery(id+"F0.imprint","INTERSECT",VERTEX,{"derivedFrom":[subQ1,subQ7]});Q65=makeQuery(id+"F0.imprint","IMPRINT",FACE,{"disambiguationData":[TD([[makeQuery(id+"F0.imprint","IMPRINT",EDGE,{"disambiguationData":[TD([[subQ8,-1.0]])],"derivedFrom":subQ1}),-1.0]])]});}
            var Q66;
            {var subQ0=sQuery(id+"F0.wireOp",EDGE,"E38");var subQ1=sQuery(id+"F0.wireOp",EDGE,"E4");var subQ2=makeQuery(id+"F0.imprint","INTERSECT",VERTEX,{"disambiguationData":[OD(0.0)],"derivedFrom":[subQ1,subQ0]});Q66=makeQuery(id+"F0.imprint","IMPRINT",FACE,{"disambiguationData":[TD([[makeQuery(id+"F0.imprint","IMPRINT",EDGE,{"disambiguationData":[TD([[subQ2,-1.0]])],"derivedFrom":subQ1}),1.0]])]});}
            var Q67;
            {var subQ5=sQuery(id+"F0.wireOp",EDGE,"E38");var subQ6=sQuery(id+"F0.wireOp",EDGE,"E4");var subQ7=makeQuery(id+"F0.imprint","INTERSECT",VERTEX,{"disambiguationData":[OD(0.0)],"derivedFrom":[subQ6,subQ5]});Q67=makeQuery(id+"F0.imprint","IMPRINT",FACE,{"disambiguationData":[TD([[makeQuery(id+"F0.imprint","IMPRINT",EDGE,{"disambiguationData":[TD([[subQ7,-1.0]])],"derivedFrom":subQ6}),-1.0]])]});}
            var Q68;
            {var subQ0=sQuery(id+"F0.wireOp",EDGE,"E38");var subQ1=sQuery(id+"F0.wireOp",EDGE,"E24");var subQ2=makeQuery(id+"F0.imprint","INTERSECT",VERTEX,{"derivedFrom":[subQ1,subQ0]});Q68=makeQuery(id+"F0.imprint","IMPRINT",FACE,{"disambiguationData":[TD([[makeQuery(id+"F0.imprint","IMPRINT",EDGE,{"disambiguationData":[TD([[subQ2,-1.0]])],"derivedFrom":subQ1}),-1.0]])]});}
            var Q69;
            {var subQ0=sQuery(id+"F0.wireOp",EDGE,"E38");var subQ1=sQuery(id+"F0.wireOp",EDGE,"E19");var subQ2=makeQuery(id+"F0.imprint","INTERSECT",VERTEX,{"derivedFrom":[subQ1,subQ0]});Q69=makeQuery(id+"F0.imprint","IMPRINT",FACE,{"disambiguationData":[TD([[makeQuery(id+"F0.imprint","IMPRINT",EDGE,{"disambiguationData":[TD([[subQ2,-1.0]])],"derivedFrom":subQ1}),1.0]])]});}
            var Q70;
            {var subQ0=sQuery(id+"F0.wireOp",EDGE,"E69");var subQ1=sQuery(id+"F0.wireOp",EDGE,"E38");var subQ2=makeQuery(id+"F0.imprint","INTERSECT",VERTEX,{"derivedFrom":[subQ1,subQ0]});Q70=makeQuery(id+"F0.imprint","IMPRINT",FACE,{"disambiguationData":[TD([[makeQuery(id+"F0.imprint","IMPRINT",EDGE,{"disambiguationData":[TD([[subQ2,-1.0]])],"derivedFrom":subQ1}),1.0]])]});}
            var Q71;
            {var subQ1=sQuery(id+"F0.wireOp",EDGE,"E25");var subQ7=sQuery(id+"F0.wireOp",EDGE,"E69");var subQ9=makeQuery(id+"F0.imprint","INTERSECT",VERTEX,{"derivedFrom":[subQ1,subQ7]});Q71=makeQuery(id+"F0.imprint","IMPRINT",FACE,{"disambiguationData":[TD([[makeQuery(id+"F0.imprint","IMPRINT",EDGE,{"disambiguationData":[TD([[subQ9,-1.0]])],"derivedFrom":subQ1}),1.0]])]});}
            var Q72;
            {var subQ1=sQuery(id+"F0.wireOp",EDGE,"E25");var subQ5=sQuery(id+"F0.wireOp",EDGE,"E63");var subQ6=makeQuery(id+"F0.imprint","INTERSECT",VERTEX,{"derivedFrom":[subQ1,subQ5]});Q72=makeQuery(id+"F0.imprint","IMPRINT",FACE,{"disambiguationData":[TD([[makeQuery(id+"F0.imprint","IMPRINT",EDGE,{"disambiguationData":[TD([[subQ6,-1.0]])],"derivedFrom":subQ1}),-1.0]])]});}
            var Q73;
            {var subQ0=sQuery(id+"F0.wireOp",EDGE,"E63");var subQ1=sQuery(id+"F0.wireOp",EDGE,"E6");var subQ2=makeQuery(id+"F0.imprint","INTERSECT",VERTEX,{"derivedFrom":[subQ1,subQ0]});Q73=makeQuery(id+"F0.imprint","IMPRINT",FACE,{"disambiguationData":[TD([[makeQuery(id+"F0.imprint","IMPRINT",EDGE,{"disambiguationData":[TD([[subQ2,-1.0]])],"derivedFrom":subQ1}),1.0]])]});}
            var Q74;
            {var subQ0=sQuery(id+"F0.wireOp",EDGE,"E30");var subQ1=sQuery(id+"F0.wireOp",EDGE,"E6");var subQ2=makeQuery(id+"F0.imprint","INTERSECT",VERTEX,{"derivedFrom":[subQ1,subQ0]});Q74=makeQuery(id+"F0.imprint","IMPRINT",FACE,{"disambiguationData":[TD([[makeQuery(id+"F0.imprint","IMPRINT",EDGE,{"disambiguationData":[TD([[subQ2,-1.0]])],"derivedFrom":subQ1}),1.0]])]});}
            var Q75;
            {var subQ0=sQuery(id+"F0.wireOp",EDGE,"E6");var subQ1=sQuery(id+"F0.wireOp",EDGE,"E4");var subQ2=makeQuery(id+"F0.imprint","INTERSECT",VERTEX,{"disambiguationData":[OD(0.0)],"derivedFrom":[subQ1,subQ0]});Q75=makeQuery(id+"F0.imprint","IMPRINT",FACE,{"disambiguationData":[TD([[makeQuery(id+"F0.imprint","IMPRINT",EDGE,{"disambiguationData":[TD([[subQ2,-1.0]])],"derivedFrom":subQ1}),1.0]])]});}
            var Q76;
            {var subQ3=sQuery(id+"F0.wireOp",EDGE,"E52");var subQ6=sQuery(id+"F0.wireOp",EDGE,"E6");var subQ9=makeQuery(id+"F0.imprint","INTERSECT",VERTEX,{"derivedFrom":[subQ6,subQ3]});Q76=makeQuery(id+"F0.imprint","IMPRINT",FACE,{"disambiguationData":[TD([[makeQuery(id+"F0.imprint","IMPRINT",EDGE,{"disambiguationData":[TD([[subQ9,-1.0]])],"derivedFrom":subQ6}),1.0]])]});}
            var Q77;
            {var subQ0=sQuery(id+"F0.wireOp",EDGE,"E49");var subQ1=sQuery(id+"F0.wireOp",EDGE,"E6");var subQ2=makeQuery(id+"F0.imprint","INTERSECT",VERTEX,{"derivedFrom":[subQ1,subQ0]});Q77=makeQuery(id+"F0.imprint","IMPRINT",FACE,{"disambiguationData":[TD([[makeQuery(id+"F0.imprint","IMPRINT",EDGE,{"disambiguationData":[TD([[subQ2,-1.0]])],"derivedFrom":subQ1}),1.0]])]});}
            var Q78;
            {var subQ0=sQuery(id+"F0.wireOp",EDGE,"E50");Q78=makeQuery(id+"F0.imprint","IMPRINT",FACE,{"disambiguationData":[TD([[makeQuery(id+"F0.imprint","IMPRINT",EDGE,{"derivedFrom":subQ0}),1.0]])]});}
            var Q79;
            {var subQ1=sQuery(id+"F0.wireOp",EDGE,"E29");var subQ5=sQuery(id+"F0.wireOp",EDGE,"E6");var subQ6=makeQuery(id+"F0.imprint","INTERSECT",VERTEX,{"derivedFrom":[subQ5,subQ1]});Q79=makeQuery(id+"F0.imprint","IMPRINT",FACE,{"disambiguationData":[TD([[makeQuery(id+"F0.imprint","IMPRINT",EDGE,{"disambiguationData":[TD([[subQ6,-1.0]])],"derivedFrom":subQ5}),-1.0]])]});}
            var Q80;
            {var subQ5=sQuery(id+"F0.wireOp",EDGE,"E50");Q80=makeQuery(id+"F0.imprint","IMPRINT",FACE,{"disambiguationData":[TD([[makeQuery(id+"F0.imprint","IMPRINT",EDGE,{"derivedFrom":subQ5}),-1.0]])]});}
            extrude(context, id + "F1", {"entities" : qUnion([Q0, Q1, Q2, Q3, Q4, Q5, Q6, Q7, Q8, Q9, Q10, Q11, Q12, Q13, Q14, Q15, Q16, Q17, Q18, Q19, Q20, Q21, Q22, Q23, Q24, Q25, Q26, Q27, Q28, Q29, Q30, Q31, Q32, Q33, Q34, Q35, Q36, Q37, Q38, Q39, Q40, Q41, Q42, Q43, Q44, Q45, Q46, Q47, Q48, Q49, Q50, Q51, Q52, Q53, Q54, Q55, Q56, Q57, Q58, Q59, Q60, Q61, Q62, Q63, Q64, Q65, Q66, Q67, Q68, Q69, Q70, Q71, Q72, Q73, Q74, Q75, Q76, Q77, Q78, Q79, Q80]), "depth" : 100 * mm});
        }
        {
            var Q0;
            {var subQ0=sQuery(id+"F0.wireOp",EDGE,"E47");var subQ1=sQuery(id+"F0.wireOp",EDGE,"E29");var subQ2=makeQuery(id+"F0.imprint","INTERSECT",VERTEX,{"derivedFrom":[subQ1,subQ0]});Q0=makeQuery(id+"F0.imprint","IMPRINT",FACE,{"disambiguationData":[TD([[makeQuery(id+"F0.imprint","IMPRINT",EDGE,{"disambiguationData":[TD([[subQ2,1.0]])],"derivedFrom":subQ1}),-1.0]])]});}
            var Q1;
            {var subQ0=sQuery(id+"F0.wireOp",EDGE,"E28");var subQ1=sQuery(id+"F0.wireOp",EDGE,"E6");var subQ2=makeQuery(id+"F0.imprint","INTERSECT",VERTEX,{"derivedFrom":[subQ1,subQ0]});Q1=makeQuery(id+"F0.imprint","IMPRINT",FACE,{"disambiguationData":[TD([[makeQuery(id+"F0.imprint","IMPRINT",EDGE,{"disambiguationData":[TD([[subQ2,-1.0]])],"derivedFrom":subQ1}),-1.0]])]});}
            var Q2;
            {var subQ0=sQuery(id+"F0.wireOp",EDGE,"E28");var subQ1=sQuery(id+"F0.wireOp",EDGE,"E6");var subQ2=makeQuery(id+"F0.imprint","INTERSECT",VERTEX,{"derivedFrom":[subQ1,subQ0]});Q2=makeQuery(id+"F0.imprint","IMPRINT",FACE,{"disambiguationData":[TD([[makeQuery(id+"F0.imprint","IMPRINT",EDGE,{"disambiguationData":[TD([[subQ2,-1.0]])],"derivedFrom":subQ1}),1.0]])]});}
            var Q3;
            {var subQ3=sQuery(id+"F0.wireOp",EDGE,"E29");var subQ5=sQuery(id+"F0.wireOp",EDGE,"E6");var subQ6=makeQuery(id+"F0.imprint","INTERSECT",VERTEX,{"derivedFrom":[subQ5,subQ3]});Q3=makeQuery(id+"F0.imprint","IMPRINT",FACE,{"disambiguationData":[TD([[makeQuery(id+"F0.imprint","IMPRINT",EDGE,{"disambiguationData":[TD([[subQ6,-1.0]])],"derivedFrom":subQ5}),1.0]])]});}
            var Q4;
            {var subQ0=sQuery(id+"F0.wireOp",EDGE,"E32");var subQ1=sQuery(id+"F0.wireOp",EDGE,"E6");var subQ2=makeQuery(id+"F0.imprint","INTERSECT",VERTEX,{"derivedFrom":[subQ1,subQ0]});Q4=makeQuery(id+"F0.imprint","IMPRINT",FACE,{"disambiguationData":[TD([[makeQuery(id+"F0.imprint","IMPRINT",EDGE,{"disambiguationData":[TD([[subQ2,-1.0]])],"derivedFrom":subQ1}),1.0]])]});}
            var Q5;
            {var subQ0=sQuery(id+"F0.wireOp",EDGE,"E32");var subQ1=sQuery(id+"F0.wireOp",EDGE,"E8");var subQ2=makeQuery(id+"F0.imprint","INTERSECT",VERTEX,{"derivedFrom":[subQ1,subQ0]});Q5=makeQuery(id+"F0.imprint","IMPRINT",FACE,{"disambiguationData":[TD([[makeQuery(id+"F0.imprint","IMPRINT",EDGE,{"disambiguationData":[TD([[subQ2,-1.0]])],"derivedFrom":subQ1}),1.0]])]});}
            var Q6;
            {var subQ0=sQuery(id+"F0.wireOp",EDGE,"E49");var subQ1=sQuery(id+"F0.wireOp",EDGE,"E8");var subQ2=makeQuery(id+"F0.imprint","INTERSECT",VERTEX,{"derivedFrom":[subQ1,subQ0]});Q6=makeQuery(id+"F0.imprint","IMPRINT",FACE,{"disambiguationData":[TD([[makeQuery(id+"F0.imprint","IMPRINT",EDGE,{"disambiguationData":[TD([[subQ2,-1.0]])],"derivedFrom":subQ1}),-1.0]])]});}
            var Q7;
            {var subQ1=sQuery(id+"F0.wireOp",EDGE,"E32");var subQ5=sQuery(id+"F0.wireOp",EDGE,"E8");var subQ6=makeQuery(id+"F0.imprint","INTERSECT",VERTEX,{"derivedFrom":[subQ5,subQ1]});Q7=makeQuery(id+"F0.imprint","IMPRINT",FACE,{"disambiguationData":[TD([[makeQuery(id+"F0.imprint","IMPRINT",EDGE,{"disambiguationData":[TD([[subQ6,-1.0]])],"derivedFrom":subQ5}),-1.0]])]});}
            var Q8;
            {var subQ0=sQuery(id+"F0.wireOp",EDGE,"E49");var subQ1=sQuery(id+"F0.wireOp",EDGE,"E28");var subQ2=makeQuery(id+"F0.imprint","INTERSECT",VERTEX,{"derivedFrom":[subQ1,subQ0]});Q8=makeQuery(id+"F0.imprint","IMPRINT",FACE,{"disambiguationData":[TD([[makeQuery(id+"F0.imprint","IMPRINT",EDGE,{"disambiguationData":[TD([[subQ2,-1.0]])],"derivedFrom":subQ1}),-1.0]])]});}
            var Q9;
            {var subQ0=sQuery(id+"F0.wireOp",EDGE,"E28");var subQ1=sQuery(id+"F0.wireOp",EDGE,"E26");var subQ2=makeQuery(id+"F0.imprint","INTERSECT",VERTEX,{"derivedFrom":[subQ1,subQ0]});Q9=makeQuery(id+"F0.imprint","IMPRINT",FACE,{"disambiguationData":[TD([[makeQuery(id+"F0.imprint","IMPRINT",EDGE,{"disambiguationData":[TD([[subQ2,-1.0]])],"derivedFrom":subQ1}),-1.0]])]});}
            var Q10;
            {var subQ0=sQuery(id+"F0.wireOp",EDGE,"E49");var subQ1=sQuery(id+"F0.wireOp",EDGE,"E28");var subQ2=makeQuery(id+"F0.imprint","INTERSECT",VERTEX,{"derivedFrom":[subQ1,subQ0]});Q10=makeQuery(id+"F0.imprint","IMPRINT",FACE,{"disambiguationData":[TD([[makeQuery(id+"F0.imprint","IMPRINT",EDGE,{"disambiguationData":[TD([[subQ2,-1.0]])],"derivedFrom":subQ1}),1.0]])]});}
            var Q11;
            {var subQ0=sQuery(id+"F0.wireOp",EDGE,"E52");var subQ1=sQuery(id+"F0.wireOp",EDGE,"E8");var subQ2=makeQuery(id+"F0.imprint","INTERSECT",VERTEX,{"derivedFrom":[subQ1,subQ0]});Q11=makeQuery(id+"F0.imprint","IMPRINT",FACE,{"disambiguationData":[TD([[makeQuery(id+"F0.imprint","IMPRINT",EDGE,{"disambiguationData":[TD([[subQ2,-1.0]])],"derivedFrom":subQ1}),-1.0]])]});}
            var Q12;
            {var subQ0=sQuery(id+"F0.wireOp",EDGE,"E29");var subQ1=sQuery(id+"F0.wireOp",EDGE,"E26");var subQ2=makeQuery(id+"F0.imprint","INTERSECT",VERTEX,{"derivedFrom":[subQ1,subQ0]});Q12=makeQuery(id+"F0.imprint","IMPRINT",FACE,{"disambiguationData":[TD([[makeQuery(id+"F0.imprint","IMPRINT",EDGE,{"disambiguationData":[TD([[subQ2,-1.0]])],"derivedFrom":subQ1}),1.0]])]});}
            var Q13;
            {var subQ1=sQuery(id+"F0.wireOp",EDGE,"E26");var subQ3=sQuery(id+"F0.wireOp",EDGE,"E29");var subQ4=makeQuery(id+"F0.imprint","INTERSECT",VERTEX,{"derivedFrom":[subQ1,subQ3]});Q13=makeQuery(id+"F0.imprint","IMPRINT",FACE,{"disambiguationData":[TD([[makeQuery(id+"F0.imprint","IMPRINT",EDGE,{"disambiguationData":[TD([[subQ4,-1.0]])],"derivedFrom":subQ3}),1.0]])]});}
            var Q14;
            {var subQ0=sQuery(id+"F0.wireOp",EDGE,"E46");var subQ1=sQuery(id+"F0.wireOp",EDGE,"E29");var subQ2=makeQuery(id+"F0.imprint","INTERSECT",VERTEX,{"derivedFrom":[subQ1,subQ0]});Q14=makeQuery(id+"F0.imprint","IMPRINT",FACE,{"disambiguationData":[TD([[makeQuery(id+"F0.imprint","IMPRINT",EDGE,{"disambiguationData":[TD([[subQ2,-1.0]])],"derivedFrom":subQ1}),-1.0]])]});}
            var Q15;
            {var subQ0=sQuery(id+"F0.wireOp",EDGE,"E49");var subQ1=sQuery(id+"F0.wireOp",EDGE,"E26");var subQ2=makeQuery(id+"F0.imprint","INTERSECT",VERTEX,{"derivedFrom":[subQ1,subQ0]});Q15=makeQuery(id+"F0.imprint","IMPRINT",FACE,{"disambiguationData":[TD([[makeQuery(id+"F0.imprint","IMPRINT",EDGE,{"disambiguationData":[TD([[subQ2,-1.0]])],"derivedFrom":subQ1}),1.0]])]});}
            var Q16;
            {var subQ0=sQuery(id+"F0.wireOp",EDGE,"E29");var subQ1=sQuery(id+"F0.wireOp",EDGE,"E26");var subQ2=makeQuery(id+"F0.imprint","INTERSECT",VERTEX,{"derivedFrom":[subQ1,subQ0]});Q16=makeQuery(id+"F0.imprint","IMPRINT",FACE,{"disambiguationData":[TD([[makeQuery(id+"F0.imprint","IMPRINT",EDGE,{"disambiguationData":[TD([[subQ2,-1.0]])],"derivedFrom":subQ1}),-1.0]])]});}
            var Q17;
            {var subQ0=sQuery(id+"F0.wireOp",EDGE,"E58");var subQ1=sQuery(id+"F0.wireOp",EDGE,"E28");var subQ2=makeQuery(id+"F0.imprint","INTERSECT",VERTEX,{"derivedFrom":[subQ1,subQ0]});Q17=makeQuery(id+"F0.imprint","IMPRINT",FACE,{"disambiguationData":[TD([[makeQuery(id+"F0.imprint","IMPRINT",EDGE,{"disambiguationData":[TD([[subQ2,-1.0]])],"derivedFrom":subQ1}),1.0]])]});}
            var Q18;
            {var subQ5=sQuery(id+"F0.wireOp",EDGE,"E28");var subQ7=sQuery(id+"F0.wireOp",EDGE,"E26");var subQ8=makeQuery(id+"F0.imprint","INTERSECT",VERTEX,{"derivedFrom":[subQ7,subQ5]});Q18=makeQuery(id+"F0.imprint","IMPRINT",FACE,{"disambiguationData":[TD([[makeQuery(id+"F0.imprint","IMPRINT",EDGE,{"disambiguationData":[TD([[subQ8,-1.0]])],"derivedFrom":subQ7}),1.0]])]});}
            var Q19;
            {var subQ1=sQuery(id+"F0.wireOp",EDGE,"E26");var subQ7=sQuery(id+"F0.wireOp",EDGE,"E44");var subQ9=makeQuery(id+"F0.imprint","INTERSECT",VERTEX,{"derivedFrom":[subQ1,subQ7]});Q19=makeQuery(id+"F0.imprint","IMPRINT",FACE,{"disambiguationData":[TD([[makeQuery(id+"F0.imprint","IMPRINT",EDGE,{"disambiguationData":[TD([[subQ9,1.0]])],"derivedFrom":subQ1}),1.0]])]});}
            var Q20;
            {var subQ0=sQuery(id+"F0.wireOp",EDGE,"E52");var subQ1=sQuery(id+"F0.wireOp",EDGE,"E31");var subQ2=makeQuery(id+"F0.imprint","INTERSECT",VERTEX,{"derivedFrom":[subQ1,subQ0]});Q20=makeQuery(id+"F0.imprint","IMPRINT",FACE,{"disambiguationData":[TD([[makeQuery(id+"F0.imprint","IMPRINT",EDGE,{"disambiguationData":[TD([[subQ2,-1.0]])],"derivedFrom":subQ1}),1.0]])]});}
            var Q21;
            {var subQ0=sQuery(id+"F0.wireOp",EDGE,"E46");var subQ1=sQuery(id+"F0.wireOp",EDGE,"E28");var subQ2=makeQuery(id+"F0.imprint","INTERSECT",VERTEX,{"derivedFrom":[subQ1,subQ0]});Q21=makeQuery(id+"F0.imprint","IMPRINT",FACE,{"disambiguationData":[TD([[makeQuery(id+"F0.imprint","IMPRINT",EDGE,{"disambiguationData":[TD([[subQ2,-1.0]])],"derivedFrom":subQ1}),1.0]])]});}
            var Q22;
            {var subQ0=sQuery(id+"F0.wireOp",EDGE,"E46");var subQ1=sQuery(id+"F0.wireOp",EDGE,"E31");var subQ2=makeQuery(id+"F0.imprint","INTERSECT",VERTEX,{"derivedFrom":[subQ1,subQ0]});Q22=makeQuery(id+"F0.imprint","IMPRINT",FACE,{"disambiguationData":[TD([[makeQuery(id+"F0.imprint","IMPRINT",EDGE,{"disambiguationData":[TD([[subQ2,-1.0]])],"derivedFrom":subQ1}),1.0]])]});}
            var Q23;
            {var subQ0=sQuery(id+"F0.wireOp",EDGE,"E46");var subQ1=sQuery(id+"F0.wireOp",EDGE,"E31");var subQ2=makeQuery(id+"F0.imprint","INTERSECT",VERTEX,{"derivedFrom":[subQ1,subQ0]});Q23=makeQuery(id+"F0.imprint","IMPRINT",FACE,{"disambiguationData":[TD([[makeQuery(id+"F0.imprint","IMPRINT",EDGE,{"disambiguationData":[TD([[subQ2,-1.0]])],"derivedFrom":subQ1}),-1.0]])]});}
            var Q24;
            {var subQ0=sQuery(id+"F0.wireOp",EDGE,"E68");var subQ1=sQuery(id+"F0.wireOp",EDGE,"E28");var subQ2=makeQuery(id+"F0.imprint","INTERSECT",VERTEX,{"derivedFrom":[subQ1,subQ0]});Q24=makeQuery(id+"F0.imprint","IMPRINT",FACE,{"disambiguationData":[TD([[makeQuery(id+"F0.imprint","IMPRINT",EDGE,{"disambiguationData":[TD([[subQ2,-1.0]])],"derivedFrom":subQ1}),1.0]])]});}
            var Q25;
            {var subQ0=sQuery(id+"F0.wireOp",EDGE,"E68");var subQ1=sQuery(id+"F0.wireOp",EDGE,"E26");var subQ2=makeQuery(id+"F0.imprint","INTERSECT",VERTEX,{"derivedFrom":[subQ1,subQ0]});Q25=makeQuery(id+"F0.imprint","IMPRINT",FACE,{"disambiguationData":[TD([[makeQuery(id+"F0.imprint","IMPRINT",EDGE,{"disambiguationData":[TD([[subQ2,-1.0]])],"derivedFrom":subQ1}),1.0]])]});}
            var Q26;
            {var subQ0=sQuery(id+"F0.wireOp",EDGE,"E68");var subQ1=sQuery(id+"F0.wireOp",EDGE,"E26");var subQ2=makeQuery(id+"F0.imprint","INTERSECT",VERTEX,{"derivedFrom":[subQ1,subQ0]});Q26=makeQuery(id+"F0.imprint","IMPRINT",FACE,{"disambiguationData":[TD([[makeQuery(id+"F0.imprint","IMPRINT",EDGE,{"disambiguationData":[TD([[subQ2,-1.0]])],"derivedFrom":subQ1}),-1.0]])]});}
            var Q27;
            {var subQ3=sQuery(id+"F0.wireOp",EDGE,"E31");var subQ5=sQuery(id+"F0.wireOp",EDGE,"E49");var subQ6=makeQuery(id+"F0.imprint","INTERSECT",VERTEX,{"derivedFrom":[subQ3,subQ5]});Q27=makeQuery(id+"F0.imprint","IMPRINT",FACE,{"disambiguationData":[TD([[makeQuery(id+"F0.imprint","IMPRINT",EDGE,{"disambiguationData":[TD([[subQ6,-1.0]])],"derivedFrom":subQ5}),1.0]])]});}
            var Q28;
            {var subQ3=sQuery(id+"F0.wireOp",EDGE,"E31");var subQ5=sQuery(id+"F0.wireOp",EDGE,"E8");var subQ6=makeQuery(id+"F0.imprint","INTERSECT",VERTEX,{"derivedFrom":[subQ5,subQ3]});Q28=makeQuery(id+"F0.imprint","IMPRINT",FACE,{"disambiguationData":[TD([[makeQuery(id+"F0.imprint","IMPRINT",EDGE,{"disambiguationData":[TD([[subQ6,-1.0]])],"derivedFrom":subQ5}),-1.0]])]});}
            var Q29;
            {var subQ0=sQuery(id+"F0.wireOp",EDGE,"E31");var subQ1=sQuery(id+"F0.wireOp",EDGE,"E26");var subQ2=makeQuery(id+"F0.imprint","INTERSECT",VERTEX,{"derivedFrom":[subQ1,subQ0]});Q29=makeQuery(id+"F0.imprint","IMPRINT",FACE,{"disambiguationData":[TD([[makeQuery(id+"F0.imprint","IMPRINT",EDGE,{"disambiguationData":[TD([[subQ2,-1.0]])],"derivedFrom":subQ1}),1.0]])]});}
            var Q30;
            {var subQ0=sQuery(id+"F0.wireOp",EDGE,"E46");var subQ1=sQuery(id+"F0.wireOp",EDGE,"E44");var subQ2=makeQuery(id+"F0.imprint","INTERSECT",VERTEX,{"derivedFrom":[subQ1,subQ0]});Q30=makeQuery(id+"F0.imprint","IMPRINT",FACE,{"disambiguationData":[TD([[makeQuery(id+"F0.imprint","IMPRINT",EDGE,{"disambiguationData":[TD([[subQ2,1.0]])],"derivedFrom":subQ1}),1.0]])]});}
            var Q31;
            {var subQ0=sQuery(id+"F0.wireOp",EDGE,"E66");var subQ1=sQuery(id+"F0.wireOp",EDGE,"E29");var subQ2=makeQuery(id+"F0.imprint","INTERSECT",VERTEX,{"derivedFrom":[subQ1,subQ0]});Q31=makeQuery(id+"F0.imprint","IMPRINT",FACE,{"disambiguationData":[TD([[makeQuery(id+"F0.imprint","IMPRINT",EDGE,{"disambiguationData":[TD([[subQ2,-1.0]])],"derivedFrom":subQ1}),-1.0]])]});}
            var Q32;
            {var subQ0=sQuery(id+"F0.wireOp",EDGE,"E67");var subQ1=sQuery(id+"F0.wireOp",EDGE,"E49");var subQ2=makeQuery(id+"F0.imprint","INTERSECT",VERTEX,{"derivedFrom":[subQ1,subQ0]});Q32=makeQuery(id+"F0.imprint","IMPRINT",FACE,{"disambiguationData":[TD([[makeQuery(id+"F0.imprint","IMPRINT",EDGE,{"disambiguationData":[TD([[subQ2,-1.0]])],"derivedFrom":subQ1}),-1.0]])]});}
            var Q33;
            {var subQ0=sQuery(id+"F0.wireOp",EDGE,"E67");var subQ1=sQuery(id+"F0.wireOp",EDGE,"E29");var subQ2=makeQuery(id+"F0.imprint","INTERSECT",VERTEX,{"derivedFrom":[subQ1,subQ0]});Q33=makeQuery(id+"F0.imprint","IMPRINT",FACE,{"disambiguationData":[TD([[makeQuery(id+"F0.imprint","IMPRINT",EDGE,{"disambiguationData":[TD([[subQ2,-1.0]])],"derivedFrom":subQ1}),-1.0]])]});}
            var Q34;
            {var subQ0=sQuery(id+"F0.wireOp",EDGE,"E67");var subQ1=sQuery(id+"F0.wireOp",EDGE,"E29");var subQ2=makeQuery(id+"F0.imprint","INTERSECT",VERTEX,{"derivedFrom":[subQ1,subQ0]});Q34=makeQuery(id+"F0.imprint","IMPRINT",FACE,{"disambiguationData":[TD([[makeQuery(id+"F0.imprint","IMPRINT",EDGE,{"disambiguationData":[TD([[subQ2,-1.0]])],"derivedFrom":subQ1}),1.0]])]});}
            var Q35;
            {var subQ0=sQuery(id+"F0.wireOp",EDGE,"E67");var subQ5=sQuery(id+"F0.wireOp",EDGE,"E46");var subQ6=makeQuery(id+"F0.imprint","INTERSECT",VERTEX,{"derivedFrom":[subQ5,subQ0]});Q35=makeQuery(id+"F0.imprint","IMPRINT",FACE,{"disambiguationData":[TD([[makeQuery(id+"F0.imprint","IMPRINT",EDGE,{"disambiguationData":[TD([[subQ6,-1.0]])],"derivedFrom":subQ5}),1.0]])]});}
            var Q36;
            {var subQ0=sQuery(id+"F0.wireOp",EDGE,"E30");var subQ5=sQuery(id+"F0.wireOp",EDGE,"E8");var subQ6=makeQuery(id+"F0.imprint","INTERSECT",VERTEX,{"derivedFrom":[subQ5,subQ0]});Q36=makeQuery(id+"F0.imprint","IMPRINT",FACE,{"disambiguationData":[TD([[makeQuery(id+"F0.imprint","IMPRINT",EDGE,{"disambiguationData":[TD([[subQ6,-1.0]])],"derivedFrom":subQ5}),-1.0]])]});}
            var Q37;
            {var subQ5=sQuery(id+"F0.wireOp",EDGE,"E43");var subQ7=sQuery(id+"F0.wireOp",EDGE,"E27");var subQ9=makeQuery(id+"F0.imprint","INTERSECT",VERTEX,{"derivedFrom":[subQ7,subQ5]});Q37=makeQuery(id+"F0.imprint","IMPRINT",FACE,{"disambiguationData":[TD([[makeQuery(id+"F0.imprint","IMPRINT",EDGE,{"disambiguationData":[TD([[subQ9,-1.0]])],"derivedFrom":subQ7}),-1.0]])]});}
            var Q38;
            {var subQ0=sQuery(id+"F0.wireOp",EDGE,"E65");var subQ1=sQuery(id+"F0.wireOp",EDGE,"E27");var subQ2=makeQuery(id+"F0.imprint","INTERSECT",VERTEX,{"derivedFrom":[subQ1,subQ0]});Q38=makeQuery(id+"F0.imprint","IMPRINT",FACE,{"disambiguationData":[TD([[makeQuery(id+"F0.imprint","IMPRINT",EDGE,{"disambiguationData":[TD([[subQ2,-1.0]])],"derivedFrom":subQ1}),-1.0]])]});}
            var Q39;
            {var subQ0=sQuery(id+"F0.wireOp",EDGE,"E27");var subQ5=sQuery(id+"F0.wireOp",EDGE,"E65");var subQ6=makeQuery(id+"F0.imprint","INTERSECT",VERTEX,{"derivedFrom":[subQ0,subQ5]});Q39=makeQuery(id+"F0.imprint","IMPRINT",FACE,{"disambiguationData":[TD([[makeQuery(id+"F0.imprint","IMPRINT",EDGE,{"disambiguationData":[TD([[subQ6,-1.0]])],"derivedFrom":subQ5}),-1.0]])]});}
            var Q40;
            {var subQ0=sQuery(id+"F0.wireOp",EDGE,"E25");var subQ5=sQuery(id+"F0.wireOp",EDGE,"E63");var subQ6=makeQuery(id+"F0.imprint","INTERSECT",VERTEX,{"derivedFrom":[subQ0,subQ5]});Q40=makeQuery(id+"F0.imprint","IMPRINT",FACE,{"disambiguationData":[TD([[makeQuery(id+"F0.imprint","IMPRINT",EDGE,{"disambiguationData":[TD([[subQ6,1.0]])],"derivedFrom":subQ5}),-1.0]])]});}
            var Q41;
            {var subQ0=sQuery(id+"F0.wireOp",EDGE,"E63");var subQ1=sQuery(id+"F0.wireOp",EDGE,"E25");var subQ2=makeQuery(id+"F0.imprint","INTERSECT",VERTEX,{"derivedFrom":[subQ1,subQ0]});Q41=makeQuery(id+"F0.imprint","IMPRINT",FACE,{"disambiguationData":[TD([[makeQuery(id+"F0.imprint","IMPRINT",EDGE,{"disambiguationData":[TD([[subQ2,-1.0]])],"derivedFrom":subQ1}),1.0]])]});}
            var Q42;
            {var subQ1=sQuery(id+"F0.wireOp",EDGE,"E25");var subQ5=sQuery(id+"F0.wireOp",EDGE,"E46");var subQ6=makeQuery(id+"F0.imprint","INTERSECT",VERTEX,{"derivedFrom":[subQ1,subQ5]});Q42=makeQuery(id+"F0.imprint","IMPRINT",FACE,{"disambiguationData":[TD([[makeQuery(id+"F0.imprint","IMPRINT",EDGE,{"disambiguationData":[TD([[subQ6,-1.0]])],"derivedFrom":subQ1}),1.0]])]});}
            var Q43;
            {var subQ1=sQuery(id+"F0.wireOp",EDGE,"E25");var subQ3=sQuery(id+"F0.wireOp",EDGE,"E65");var subQ4=makeQuery(id+"F0.imprint","INTERSECT",VERTEX,{"derivedFrom":[subQ1,subQ3]});Q43=makeQuery(id+"F0.imprint","IMPRINT",FACE,{"disambiguationData":[TD([[makeQuery(id+"F0.imprint","IMPRINT",EDGE,{"disambiguationData":[TD([[subQ4,-1.0]])],"derivedFrom":subQ3}),-1.0]])]});}
            var Q44;
            {var subQ1=sQuery(id+"F0.wireOp",EDGE,"E25");var subQ3=sQuery(id+"F0.wireOp",EDGE,"E63");var subQ4=makeQuery(id+"F0.imprint","INTERSECT",VERTEX,{"derivedFrom":[subQ1,subQ3]});Q44=makeQuery(id+"F0.imprint","IMPRINT",FACE,{"disambiguationData":[TD([[makeQuery(id+"F0.imprint","IMPRINT",EDGE,{"disambiguationData":[TD([[subQ4,-1.0]])],"derivedFrom":subQ3}),-1.0]])]});}
            var Q45;
            {var subQ0=sQuery(id+"F0.wireOp",EDGE,"E20");var subQ1=sQuery(id+"F0.wireOp",EDGE,"E4");var subQ2=makeQuery(id+"F0.imprint","INTERSECT",VERTEX,{"derivedFrom":[subQ1,subQ0]});Q45=makeQuery(id+"F0.imprint","IMPRINT",FACE,{"disambiguationData":[TD([[makeQuery(id+"F0.imprint","IMPRINT",EDGE,{"disambiguationData":[TD([[subQ2,-1.0]])],"derivedFrom":subQ1}),-1.0]])]});}
            var Q46;
            {var subQ0=sQuery(id+"F0.wireOp",EDGE,"E63");var subQ1=sQuery(id+"F0.wireOp",EDGE,"E4");var subQ2=makeQuery(id+"F0.imprint","INTERSECT",VERTEX,{"derivedFrom":[subQ1,subQ0]});Q46=makeQuery(id+"F0.imprint","IMPRINT",FACE,{"disambiguationData":[TD([[makeQuery(id+"F0.imprint","IMPRINT",EDGE,{"disambiguationData":[TD([[subQ2,-1.0]])],"derivedFrom":subQ1}),-1.0]])]});}
            var Q47;
            {var subQ3=sQuery(id+"F0.wireOp",EDGE,"E46");var subQ5=sQuery(id+"F0.wireOp",EDGE,"E65");var subQ6=makeQuery(id+"F0.imprint","INTERSECT",VERTEX,{"derivedFrom":[subQ3,subQ5]});Q47=makeQuery(id+"F0.imprint","IMPRINT",FACE,{"disambiguationData":[TD([[makeQuery(id+"F0.imprint","IMPRINT",EDGE,{"disambiguationData":[TD([[subQ6,-1.0]])],"derivedFrom":subQ5}),-1.0]])]});}
            var Q48;
            {var subQ3=sQuery(id+"F0.wireOp",EDGE,"E43");var subQ5=sQuery(id+"F0.wireOp",EDGE,"E63");var subQ6=makeQuery(id+"F0.imprint","INTERSECT",VERTEX,{"derivedFrom":[subQ3,subQ5]});Q48=makeQuery(id+"F0.imprint","IMPRINT",FACE,{"disambiguationData":[TD([[makeQuery(id+"F0.imprint","IMPRINT",EDGE,{"disambiguationData":[TD([[subQ6,1.0]])],"derivedFrom":subQ5}),-1.0]])]});}
            var Q49;
            {var subQ0=sQuery(id+"F0.wireOp",EDGE,"E65");var subQ1=sQuery(id+"F0.wireOp",EDGE,"E43");var subQ2=makeQuery(id+"F0.imprint","INTERSECT",VERTEX,{"derivedFrom":[subQ1,subQ0]});Q49=makeQuery(id+"F0.imprint","IMPRINT",FACE,{"disambiguationData":[TD([[makeQuery(id+"F0.imprint","IMPRINT",EDGE,{"disambiguationData":[TD([[subQ2,-1.0]])],"derivedFrom":subQ0}),-1.0]])]});}
            var Q50;
            {var subQ0=sQuery(id+"F0.wireOp",EDGE,"E63");var subQ1=sQuery(id+"F0.wireOp",EDGE,"E43");var subQ2=makeQuery(id+"F0.imprint","INTERSECT",VERTEX,{"derivedFrom":[subQ1,subQ0]});Q50=makeQuery(id+"F0.imprint","IMPRINT",FACE,{"disambiguationData":[TD([[makeQuery(id+"F0.imprint","IMPRINT",EDGE,{"disambiguationData":[TD([[subQ2,-1.0]])],"derivedFrom":subQ0}),-1.0]])]});}
            var Q51;
            {var subQ0=sQuery(id+"F0.wireOp",EDGE,"E20");var subQ1=sQuery(id+"F0.wireOp",EDGE,"E4");var subQ2=makeQuery(id+"F0.imprint","INTERSECT",VERTEX,{"derivedFrom":[subQ1,subQ0]});Q51=makeQuery(id+"F0.imprint","IMPRINT",FACE,{"disambiguationData":[TD([[makeQuery(id+"F0.imprint","IMPRINT",EDGE,{"disambiguationData":[TD([[subQ2,-1.0]])],"derivedFrom":subQ1}),1.0]])]});}
            var Q52;
            {var subQ0=sQuery(id+"F0.wireOp",EDGE,"E63");var subQ1=sQuery(id+"F0.wireOp",EDGE,"E4");var subQ2=makeQuery(id+"F0.imprint","INTERSECT",VERTEX,{"derivedFrom":[subQ1,subQ0]});Q52=makeQuery(id+"F0.imprint","IMPRINT",FACE,{"disambiguationData":[TD([[makeQuery(id+"F0.imprint","IMPRINT",EDGE,{"disambiguationData":[TD([[subQ2,-1.0]])],"derivedFrom":subQ1}),1.0]])]});}
            var Q53;
            {var subQ0=sQuery(id+"F0.wireOp",EDGE,"E66");var subQ1=sQuery(id+"F0.wireOp",EDGE,"E6");var subQ2=makeQuery(id+"F0.imprint","INTERSECT",VERTEX,{"derivedFrom":[subQ1,subQ0]});Q53=makeQuery(id+"F0.imprint","IMPRINT",FACE,{"disambiguationData":[TD([[makeQuery(id+"F0.imprint","IMPRINT",EDGE,{"disambiguationData":[TD([[subQ2,-1.0]])],"derivedFrom":subQ1}),1.0]])]});}
            var Q54;
            {var subQ0=sQuery(id+"F0.wireOp",EDGE,"E68");var subQ1=sQuery(id+"F0.wireOp",EDGE,"E6");var subQ2=makeQuery(id+"F0.imprint","INTERSECT",VERTEX,{"derivedFrom":[subQ1,subQ0]});Q54=makeQuery(id+"F0.imprint","IMPRINT",FACE,{"disambiguationData":[TD([[makeQuery(id+"F0.imprint","IMPRINT",EDGE,{"disambiguationData":[TD([[subQ2,-1.0]])],"derivedFrom":subQ1}),1.0]])]});}
            var Q55;
            {var subQ0=sQuery(id+"F0.wireOp",EDGE,"E65");var subQ1=sQuery(id+"F0.wireOp",EDGE,"E6");var subQ2=makeQuery(id+"F0.imprint","INTERSECT",VERTEX,{"derivedFrom":[subQ1,subQ0]});Q55=makeQuery(id+"F0.imprint","IMPRINT",FACE,{"disambiguationData":[TD([[makeQuery(id+"F0.imprint","IMPRINT",EDGE,{"disambiguationData":[TD([[subQ2,-1.0]])],"derivedFrom":subQ1}),1.0]])]});}
            var Q56;
            {var subQ0=sQuery(id+"F0.wireOp",EDGE,"E20");var subQ1=sQuery(id+"F0.wireOp",EDGE,"E6");var subQ2=makeQuery(id+"F0.imprint","INTERSECT",VERTEX,{"derivedFrom":[subQ1,subQ0]});Q56=makeQuery(id+"F0.imprint","IMPRINT",FACE,{"disambiguationData":[TD([[makeQuery(id+"F0.imprint","IMPRINT",EDGE,{"disambiguationData":[TD([[subQ2,-1.0]])],"derivedFrom":subQ1}),1.0]])]});}
            var Q57;
            {var subQ0=sQuery(id+"F0.wireOp",EDGE,"E24");var subQ3=sQuery(id+"F0.wireOp",EDGE,"E36");var subQ5=makeQuery(id+"F0.imprint","INTERSECT",VERTEX,{"derivedFrom":[subQ0,subQ3]});Q57=makeQuery(id+"F0.imprint","IMPRINT",FACE,{"disambiguationData":[TD([[makeQuery(id+"F0.imprint","IMPRINT",EDGE,{"disambiguationData":[TD([[subQ5,1.0]])],"derivedFrom":subQ0}),-1.0]])]});}
            var Q58;
            {var subQ0=sQuery(id+"F0.wireOp",EDGE,"E70");var subQ1=sQuery(id+"F0.wireOp",EDGE,"E22");var subQ2=makeQuery(id+"F0.imprint","INTERSECT",VERTEX,{"derivedFrom":[subQ1,subQ0]});Q58=makeQuery(id+"F0.imprint","IMPRINT",FACE,{"disambiguationData":[TD([[makeQuery(id+"F0.imprint","IMPRINT",EDGE,{"disambiguationData":[TD([[subQ2,-1.0]])],"derivedFrom":subQ1}),1.0]])]});}
            var Q59;
            {var subQ0=sQuery(id+"F0.wireOp",EDGE,"E24");var subQ5=sQuery(id+"F0.wireOp",EDGE,"E38");var subQ6=makeQuery(id+"F0.imprint","INTERSECT",VERTEX,{"derivedFrom":[subQ0,subQ5]});Q59=makeQuery(id+"F0.imprint","IMPRINT",FACE,{"disambiguationData":[TD([[makeQuery(id+"F0.imprint","IMPRINT",EDGE,{"disambiguationData":[TD([[subQ6,-1.0]])],"derivedFrom":subQ5}),-1.0]])]});}
            var Q60;
            {var subQ0=sQuery(id+"F0.wireOp",EDGE,"E43");var subQ1=sQuery(id+"F0.wireOp",EDGE,"E41");var subQ2=makeQuery(id+"F0.imprint","INTERSECT",VERTEX,{"derivedFrom":[subQ1,subQ0]});Q60=makeQuery(id+"F0.imprint","IMPRINT",FACE,{"disambiguationData":[TD([[makeQuery(id+"F0.imprint","IMPRINT",EDGE,{"disambiguationData":[TD([[subQ2,1.0]])],"derivedFrom":subQ1}),-1.0]])]});}
            var Q61;
            {var subQ0=sQuery(id+"F0.wireOp",EDGE,"E18");var subQ5=sQuery(id+"F0.wireOp",EDGE,"E38");var subQ7=makeQuery(id+"F0.imprint","INTERSECT",VERTEX,{"derivedFrom":[subQ0,subQ5]});Q61=makeQuery(id+"F0.imprint","IMPRINT",FACE,{"disambiguationData":[TD([[makeQuery(id+"F0.imprint","IMPRINT",EDGE,{"disambiguationData":[TD([[subQ7,-1.0]])],"derivedFrom":subQ5}),1.0]])]});}
            var Q62;
            {var subQ0=sQuery(id+"F0.wireOp",EDGE,"E22");var subQ5=sQuery(id+"F0.wireOp",EDGE,"E70");var subQ7=makeQuery(id+"F0.imprint","INTERSECT",VERTEX,{"derivedFrom":[subQ0,subQ5]});Q62=makeQuery(id+"F0.imprint","IMPRINT",FACE,{"disambiguationData":[TD([[makeQuery(id+"F0.imprint","IMPRINT",EDGE,{"disambiguationData":[TD([[subQ7,-1.0]])],"derivedFrom":subQ5}),1.0]])]});}
            var Q63;
            {var subQ3=sQuery(id+"F0.wireOp",EDGE,"E24");var subQ5=sQuery(id+"F0.wireOp",EDGE,"E70");var subQ7=makeQuery(id+"F0.imprint","INTERSECT",VERTEX,{"derivedFrom":[subQ3,subQ5]});Q63=makeQuery(id+"F0.imprint","IMPRINT",FACE,{"disambiguationData":[TD([[makeQuery(id+"F0.imprint","IMPRINT",EDGE,{"disambiguationData":[TD([[subQ7,1.0]])],"derivedFrom":subQ5}),1.0]])]});}
            var Q64;
            {var subQ0=sQuery(id+"F0.wireOp",EDGE,"E58");var subQ1=sQuery(id+"F0.wireOp",EDGE,"E18");var subQ2=makeQuery(id+"F0.imprint","INTERSECT",VERTEX,{"derivedFrom":[subQ1,subQ0]});Q64=makeQuery(id+"F0.imprint","IMPRINT",FACE,{"disambiguationData":[TD([[makeQuery(id+"F0.imprint","IMPRINT",EDGE,{"disambiguationData":[TD([[subQ2,1.0]])],"derivedFrom":subQ0}),1.0]])]});}
            var Q65;
            {var subQ0=sQuery(id+"F0.wireOp",EDGE,"E38");var subQ1=sQuery(id+"F0.wireOp",EDGE,"E19");var subQ2=makeQuery(id+"F0.imprint","INTERSECT",VERTEX,{"derivedFrom":[subQ1,subQ0]});Q65=makeQuery(id+"F0.imprint","IMPRINT",FACE,{"disambiguationData":[TD([[makeQuery(id+"F0.imprint","IMPRINT",EDGE,{"disambiguationData":[TD([[subQ2,-1.0]])],"derivedFrom":subQ1}),-1.0]])]});}
            var Q66;
            {var subQ0=sQuery(id+"F0.wireOp",EDGE,"E43");var subQ1=sQuery(id+"F0.wireOp",EDGE,"E19");var subQ2=makeQuery(id+"F0.imprint","INTERSECT",VERTEX,{"derivedFrom":[subQ1,subQ0]});Q66=makeQuery(id+"F0.imprint","IMPRINT",FACE,{"disambiguationData":[TD([[makeQuery(id+"F0.imprint","IMPRINT",EDGE,{"disambiguationData":[TD([[subQ2,-1.0]])],"derivedFrom":subQ1}),-1.0]])]});}
            var Q67;
            {var subQ1=sQuery(id+"F0.wireOp",EDGE,"E19");var subQ3=sQuery(id+"F0.wireOp",EDGE,"E43");var subQ4=makeQuery(id+"F0.imprint","INTERSECT",VERTEX,{"derivedFrom":[subQ1,subQ3]});Q67=makeQuery(id+"F0.imprint","IMPRINT",FACE,{"disambiguationData":[TD([[makeQuery(id+"F0.imprint","IMPRINT",EDGE,{"disambiguationData":[TD([[subQ4,1.0]])],"derivedFrom":subQ3}),1.0]])]});}
            var Q68;
            {var subQ3=sQuery(id+"F0.wireOp",EDGE,"E69");var subQ5=sQuery(id+"F0.wireOp",EDGE,"E8");var subQ7=makeQuery(id+"F0.imprint","INTERSECT",VERTEX,{"derivedFrom":[subQ5,subQ3]});Q68=makeQuery(id+"F0.imprint","IMPRINT",FACE,{"disambiguationData":[TD([[makeQuery(id+"F0.imprint","IMPRINT",EDGE,{"disambiguationData":[TD([[subQ7,-1.0]])],"derivedFrom":subQ5}),-1.0]])]});}
            var Q69;
            {var subQ0=sQuery(id+"F0.wireOp",EDGE,"E70");var subQ1=sQuery(id+"F0.wireOp",EDGE,"E8");var subQ2=makeQuery(id+"F0.imprint","INTERSECT",VERTEX,{"derivedFrom":[subQ1,subQ0]});Q69=makeQuery(id+"F0.imprint","IMPRINT",FACE,{"disambiguationData":[TD([[makeQuery(id+"F0.imprint","IMPRINT",EDGE,{"disambiguationData":[TD([[subQ2,-1.0]])],"derivedFrom":subQ1}),-1.0]])]});}
            var Q70;
            {var subQ0=sQuery(id+"F0.wireOp",EDGE,"E39");var subQ1=sQuery(id+"F0.wireOp",EDGE,"E19");var subQ2=makeQuery(id+"F0.imprint","INTERSECT",VERTEX,{"derivedFrom":[subQ1,subQ0]});Q70=makeQuery(id+"F0.imprint","IMPRINT",FACE,{"disambiguationData":[TD([[makeQuery(id+"F0.imprint","IMPRINT",EDGE,{"disambiguationData":[TD([[subQ2,-1.0]])],"derivedFrom":subQ1}),-1.0]])]});}
            var Q71;
            {var subQ0=sQuery(id+"F0.wireOp",EDGE,"E41");var subQ1=sQuery(id+"F0.wireOp",EDGE,"E24");var subQ2=makeQuery(id+"F0.imprint","INTERSECT",VERTEX,{"derivedFrom":[subQ1,subQ0]});Q71=makeQuery(id+"F0.imprint","IMPRINT",FACE,{"disambiguationData":[TD([[makeQuery(id+"F0.imprint","IMPRINT",EDGE,{"disambiguationData":[TD([[subQ2,-1.0]])],"derivedFrom":subQ1}),-1.0]])]});}
            var Q72;
            {var subQ0=sQuery(id+"F0.wireOp",EDGE,"E22");var subQ1=sQuery(id+"F0.wireOp",EDGE,"E5");var subQ2=makeQuery(id+"F0.imprint","INTERSECT",VERTEX,{"derivedFrom":[subQ1,subQ0]});Q72=makeQuery(id+"F0.imprint","IMPRINT",FACE,{"disambiguationData":[TD([[makeQuery(id+"F0.imprint","IMPRINT",EDGE,{"disambiguationData":[TD([[subQ2,1.0]])],"derivedFrom":subQ1}),1.0]])]});}
            var Q73;
            {var subQ0=sQuery(id+"F0.wireOp",EDGE,"E73");var subQ1=sQuery(id+"F0.wireOp",EDGE,"E4");var subQ2=makeQuery(id+"F0.imprint","INTERSECT",VERTEX,{"derivedFrom":[subQ1,subQ0]});Q73=makeQuery(id+"F0.imprint","IMPRINT",FACE,{"disambiguationData":[TD([[makeQuery(id+"F0.imprint","IMPRINT",EDGE,{"disambiguationData":[TD([[subQ2,-1.0]])],"derivedFrom":subQ1}),1.0]])]});}
            var Q74;
            {var subQ0=sQuery(id+"F0.wireOp",EDGE,"E73");var subQ1=sQuery(id+"F0.wireOp",EDGE,"E4");var subQ2=makeQuery(id+"F0.imprint","INTERSECT",VERTEX,{"derivedFrom":[subQ1,subQ0]});Q74=makeQuery(id+"F0.imprint","IMPRINT",FACE,{"disambiguationData":[TD([[makeQuery(id+"F0.imprint","IMPRINT",EDGE,{"disambiguationData":[TD([[subQ2,-1.0]])],"derivedFrom":subQ1}),-1.0]])]});}
            var Q75;
            {var subQ0=sQuery(id+"F0.wireOp",EDGE,"E39");var subQ1=sQuery(id+"F0.wireOp",EDGE,"E24");var subQ2=makeQuery(id+"F0.imprint","INTERSECT",VERTEX,{"derivedFrom":[subQ1,subQ0]});Q75=makeQuery(id+"F0.imprint","IMPRINT",FACE,{"disambiguationData":[TD([[makeQuery(id+"F0.imprint","IMPRINT",EDGE,{"disambiguationData":[TD([[subQ2,-1.0]])],"derivedFrom":subQ1}),-1.0]])]});}
            var Q76;
            {var subQ0=sQuery(id+"F0.wireOp",EDGE,"E72");var subQ1=sQuery(id+"F0.wireOp",EDGE,"E6");var subQ2=makeQuery(id+"F0.imprint","INTERSECT",VERTEX,{"derivedFrom":[subQ1,subQ0]});Q76=makeQuery(id+"F0.imprint","IMPRINT",FACE,{"disambiguationData":[TD([[makeQuery(id+"F0.imprint","IMPRINT",EDGE,{"disambiguationData":[TD([[subQ2,-1.0]])],"derivedFrom":subQ1}),1.0]])]});}
            var Q77;
            {var subQ0=sQuery(id+"F0.wireOp",EDGE,"E71");var subQ1=sQuery(id+"F0.wireOp",EDGE,"E6");var subQ2=makeQuery(id+"F0.imprint","INTERSECT",VERTEX,{"derivedFrom":[subQ1,subQ0]});Q77=makeQuery(id+"F0.imprint","IMPRINT",FACE,{"disambiguationData":[TD([[makeQuery(id+"F0.imprint","IMPRINT",EDGE,{"disambiguationData":[TD([[subQ2,-1.0]])],"derivedFrom":subQ1}),1.0]])]});}
            extrude(context, id + "F2", {"entities" : qUnion([Q0, Q1, Q2, Q3, Q4, Q5, Q6, Q7, Q8, Q9, Q10, Q11, Q12, Q13, Q14, Q15, Q16, Q17, Q18, Q19, Q20, Q21, Q22, Q23, Q24, Q25, Q26, Q27, Q28, Q29, Q30, Q31, Q32, Q33, Q34, Q35, Q36, Q37, Q38, Q39, Q40, Q41, Q42, Q43, Q44, Q45, Q46, Q47, Q48, Q49, Q50, Q51, Q52, Q53, Q54, Q55, Q56, Q57, Q58, Q59, Q60, Q61, Q62, Q63, Q64, Q65, Q66, Q67, Q68, Q69, Q70, Q71, Q72, Q73, Q74, Q75, Q76, Q77]), "depth" : 100 * mm});
        }
    });
